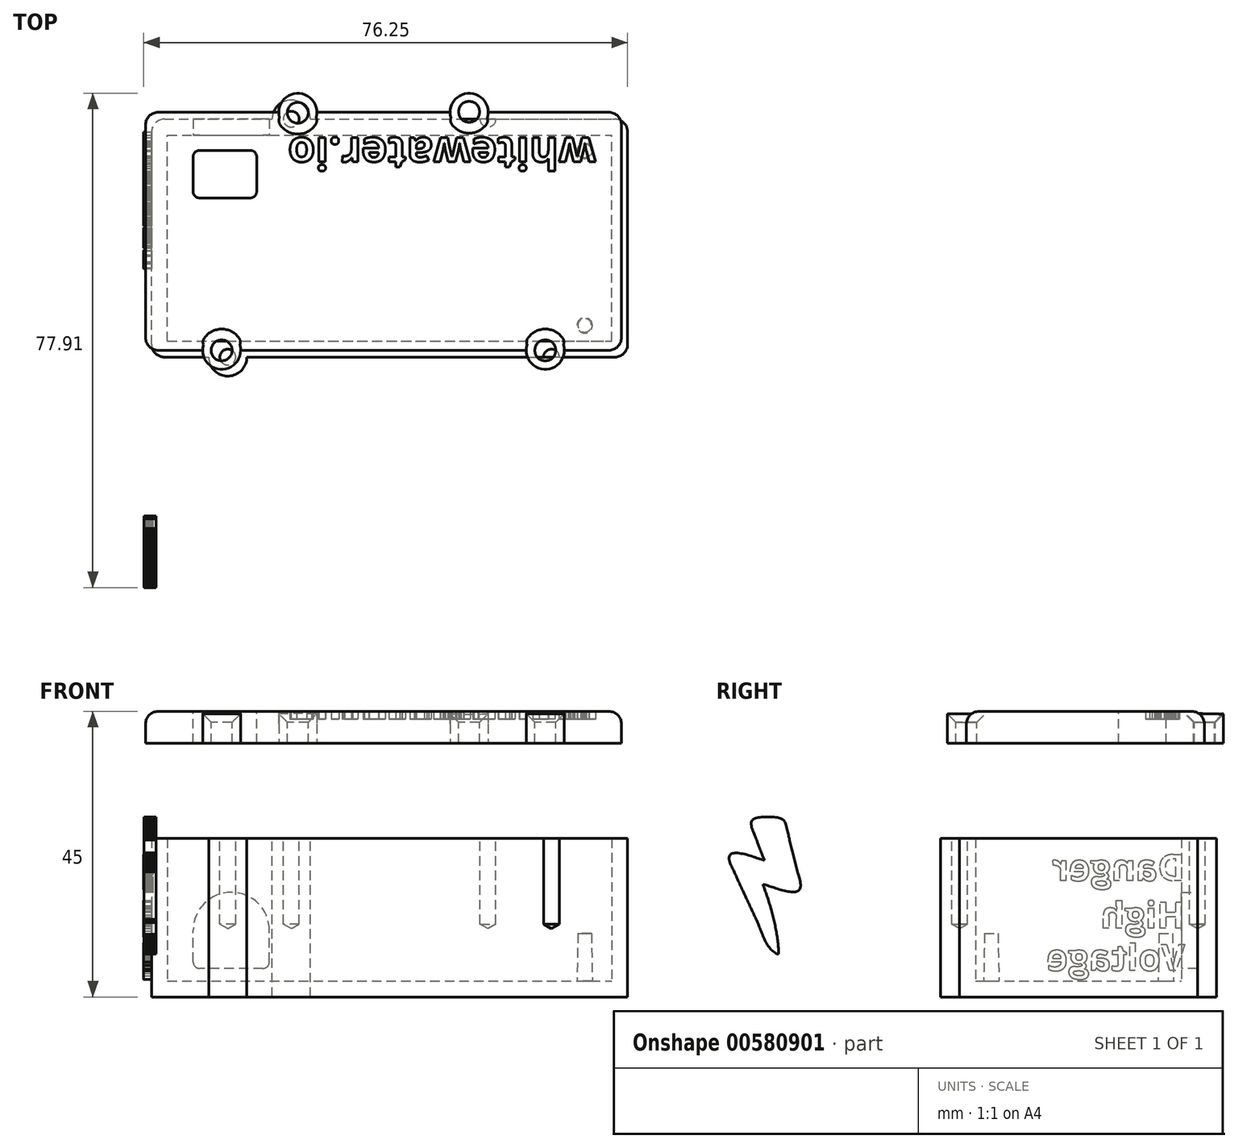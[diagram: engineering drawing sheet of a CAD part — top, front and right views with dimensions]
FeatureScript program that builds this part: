
annotation { "Feature Type Name" : "Feature", "Feature Type Description" : "" }
export const myFeature = defineFeature(function(context is Context, id is Id, definition is map)
    precondition{}
    {
        {
            var Q0;
            Q0=qCreatedBy(makeId("Front.planeOp"),FACE);
            var sketch = newSketch(context, id + "F0", { "sketchPlane" : qUnion([Q0])});
            skLineSegment(sketch, "E0.bottom", {"start": v(-37.5, -18.75) * mm, "end": v(37.5, -18.75) * mm});
            skLineSegment(sketch, "E0.top", {"start": v(-37.5, 18.75) * mm, "end": v(37.5, 18.75) * mm});
            skLineSegment(sketch, "E0.left", {"start": v(-37.5, -18.75) * mm, "end": v(-37.5, 18.75) * mm});
            skLineSegment(sketch, "E0.right", {"start": v(37.5, -18.75) * mm, "end": v(37.5, 18.75) * mm});
            skSolve(sketch);
        }
        {
            var Q0;
            Q0 = qSketchRegion(id + "F0", true);
            extrude(context, id + "F1", {"entities" : qUnion([Q0]), "depth" : 25 * mm, "offsetDistance" : 25 * mm});
        }
        {
            var Q0;
            Q0=makeQuery(id+"F1.opExtrude","CAP_FACE",FACE,{"disambiguationData":[OSD([sQuery(id+"F0.wireOp",EDGE,"E0.bottom"),sQuery(id+"F0.wireOp",EDGE,"E0.top"),sQuery(id+"F0.wireOp",EDGE,"E0.left"),sQuery(id+"F0.wireOp",EDGE,"E0.right")])],"isStart":false});
            shell(context, id + "F2", {"entities" : qUnion([Q0]), "thickness" : 2.5 * mm});
        }
        {
            var Q0;
            Q0=makeQuery(id+"F1.opExtrude","SWEPT_EDGE",EDGE,{"disambiguationData":[OSD([sQuery(id+"F0.wireOp",EDGE,"E0.bottom"),sQuery(id+"F0.wireOp",EDGE,"E0.left")])]});
            var Q1;
            Q1=makeQuery(id+"F1.opExtrude","SWEPT_EDGE",EDGE,{"disambiguationData":[OSD([sQuery(id+"F0.wireOp",EDGE,"E0.top"),sQuery(id+"F0.wireOp",EDGE,"E0.right")])]});
            var Q2;
            Q2=makeQuery(id+"F1.opExtrude","SWEPT_EDGE",EDGE,{"disambiguationData":[OSD([sQuery(id+"F0.wireOp",EDGE,"E0.bottom"),sQuery(id+"F0.wireOp",EDGE,"E0.right")])]});
            var Q3;
            Q3=makeQuery(id+"F1.opExtrude","SWEPT_EDGE",EDGE,{"disambiguationData":[OSD([sQuery(id+"F0.wireOp",EDGE,"E0.top"),sQuery(id+"F0.wireOp",EDGE,"E0.left")])]});
            fillet(context, id + "F3", {"entities" : qUnion([Q0, Q1, Q2, Q3]), "radius" : 2 * mm, "tangentPropagation" : true, "allowEdgeOverflow" : false});
        }
        {
            var Q0;
            Q0=makeQuery(id+"F2.opShell","OFFSET_FACE",FACE,{"disambiguationData":[OSD([sQuery(id+"F0.wireOp",EDGE,"E0.bottom"),sQuery(id+"F0.wireOp",EDGE,"E0.top"),sQuery(id+"F0.wireOp",EDGE,"E0.left"),sQuery(id+"F0.wireOp",EDGE,"E0.right")])]});
            var sketch = newSketch(context, id + "F4", { "sketchPlane" : qUnion([Q0])});
            skLineSegment(sketch, "E1.bottom", {"start": v(-32, 15.5) * mm, "end": v(32, 15.5) * mm, "construction": true});
            skLineSegment(sketch, "E1.top", {"start": v(-32, -15.5) * mm, "end": v(32, -15.5) * mm, "construction": true});
            skLineSegment(sketch, "E1.left", {"start": v(-32, 15.5) * mm, "end": v(-32, -15.5) * mm, "construction": true});
            skLineSegment(sketch, "E1.right", {"start": v(32, 15.5) * mm, "end": v(32, -15.5) * mm, "construction": true});
            skPoint(sketch, "E2", {"position": v(30.75, 13.75) * mm});
            skPoint(sketch, "E3.MirrorP", {"position": v(30.75, -13.75) * mm});
            skCircle(sketch, "E4", {"center": v(30.75, 13.75) * mm, "radius": 1.2 * mm});
            skCircle(sketch, "E5", {"center": v(30.75, -13.75) * mm, "radius": 1.2 * mm});
            skSolve(sketch);
        }
        {
            var Q0;
            Q0=makeQuery(id+"F4.imprint","IMPRINT",FACE,{"disambiguationData":[TD([[makeQuery(id+"F4.imprint","IMPRINT",EDGE,{"derivedFrom":sQuery(id+"F4.wireOp",EDGE,"E5")}),1.0]])]});
            var Q1;
            Q1=makeQuery(id+"F4.imprint","IMPRINT",FACE,{"disambiguationData":[TD([[makeQuery(id+"F4.imprint","IMPRINT",EDGE,{"derivedFrom":sQuery(id+"F4.wireOp",EDGE,"E4")}),1.0]])]});
            extrude(context, id + "F5", {"entities" : qUnion([Q0, Q1]), "operationType" : NewBodyOperationType.ADD, "depth" : 7.5 * mm, "offsetDistance" : 25 * mm, "hasDraft" : true, "draftAngle" : 1 * degree, "draftPullDirection" : true});
        }
        {
            var Q0;
            Q0=makeQuery(id+"F1.opExtrude","SWEPT_FACE",FACE,{"disambiguationData":[OSD([sQuery(id+"F0.wireOp",EDGE,"E0.left")])]});
            var sketch = newSketch(context, id + "F6", { "sketchPlane" : qUnion([Q0])});
            skLineSegment(sketch, "E6", {"start": v(1, 1) * mm, "end": v(0.67, 0.13) * mm});
            skLineSegment(sketch, "E7", {"start": v(0.67, 0.13) * mm, "end": v(0.35, -0.76) * mm});
            skLineSegment(sketch, "E8", {"start": v(0.35, -0.76) * mm, "end": v(0.02, -1.66) * mm});
            skLineSegment(sketch, "E9", {"start": v(0.02, -1.66) * mm, "end": v(-0.3, -2.56) * mm});
            skLineSegment(sketch, "E10", {"start": v(-0.3, -2.56) * mm, "end": v(-0.63, -3.48) * mm});
            skLineSegment(sketch, "E11", {"start": v(-0.63, -3.48) * mm, "end": v(-0.95, -4.4) * mm});
            skLineSegment(sketch, "E12", {"start": v(-0.95, -4.4) * mm, "end": v(-1.27, -5.34) * mm});
            skLineSegment(sketch, "E13", {"start": v(-1.27, -5.34) * mm, "end": v(-1.59, -6.29) * mm});
            skLineSegment(sketch, "E14", {"start": v(-1.59, -6.29) * mm, "end": v(-1.9, -7.24) * mm});
            skLineSegment(sketch, "E15", {"start": v(-1.9, -7.24) * mm, "end": v(-2.21, -8.2) * mm});
            skLineSegment(sketch, "E16", {"start": v(-2.21, -8.2) * mm, "end": v(-2.52, -9.17) * mm});
            skLineSegment(sketch, "E17", {"start": v(-2.52, -9.17) * mm, "end": v(-2.82, -10.14) * mm});
            skLineSegment(sketch, "E18", {"start": v(-2.82, -10.14) * mm, "end": v(-3.12, -11.12) * mm});
            skLineSegment(sketch, "E19", {"start": v(-3.12, -11.12) * mm, "end": v(-3.42, -12.1) * mm});
            skLineSegment(sketch, "E20", {"start": v(-3.42, -12.1) * mm, "end": v(-3.71, -13.1) * mm});
            skLineSegment(sketch, "E21", {"start": v(-3.71, -13.1) * mm, "end": v(-4, -14.1) * mm});
            skLineSegment(sketch, "E22", {"start": v(-4, -14.1) * mm, "end": v(-4.28, -15.1) * mm});
            skLineSegment(sketch, "E23", {"start": v(-4.28, -15.1) * mm, "end": v(-4.56, -16.1) * mm});
            skLineSegment(sketch, "E24", {"start": v(-4.56, -16.1) * mm, "end": v(-4.83, -17.1) * mm});
            skLineSegment(sketch, "E25", {"start": v(-4.83, -17.1) * mm, "end": v(-5.1, -18.12) * mm});
            skLineSegment(sketch, "E26", {"start": v(-5.1, -18.12) * mm, "end": v(-5.36, -19.13) * mm});
            skLineSegment(sketch, "E27", {"start": v(-5.36, -19.13) * mm, "end": v(-5.61, -20.15) * mm});
            skLineSegment(sketch, "E28", {"start": v(-5.61, -20.15) * mm, "end": v(-5.86, -21.16) * mm});
            skLineSegment(sketch, "E29", {"start": v(-5.86, -21.16) * mm, "end": v(-6.1, -22.18) * mm});
            skLineSegment(sketch, "E30", {"start": v(-6.1, -22.18) * mm, "end": v(-6.33, -23.2) * mm});
            skLineSegment(sketch, "E31", {"start": v(-6.33, -23.2) * mm, "end": v(-6.55, -24.22) * mm});
            skLineSegment(sketch, "E32", {"start": v(-6.55, -24.22) * mm, "end": v(-6.77, -25.24) * mm});
            skLineSegment(sketch, "E33", {"start": v(-6.77, -25.24) * mm, "end": v(-6.98, -26.26) * mm});
            skLineSegment(sketch, "E34", {"start": v(-6.98, -26.26) * mm, "end": v(-7.18, -27.27) * mm});
            skLineSegment(sketch, "E35", {"start": v(-7.18, -27.27) * mm, "end": v(-7.37, -28.29) * mm});
            skLineSegment(sketch, "E36", {"start": v(-7.37, -28.29) * mm, "end": v(-7.55, -29.3) * mm});
            skLineSegment(sketch, "E37", {"start": v(-7.55, -29.3) * mm, "end": v(-7.73, -30.31) * mm});
            skLineSegment(sketch, "E38", {"start": v(-7.73, -30.31) * mm, "end": v(-7.9, -31.32) * mm});
            skLineSegment(sketch, "E39", {"start": v(-7.9, -31.32) * mm, "end": v(-8.04, -32.32) * mm});
            skLineSegment(sketch, "E40", {"start": v(-8.04, -32.32) * mm, "end": v(-8.19, -33.32) * mm});
            skLineSegment(sketch, "E41", {"start": v(-8.19, -33.32) * mm, "end": v(-8.32, -34.32) * mm});
            skLineSegment(sketch, "E42", {"start": v(-8.32, -34.32) * mm, "end": v(-8.44, -35.3) * mm});
            skLineSegment(sketch, "E43", {"start": v(-8.44, -35.3) * mm, "end": v(-8.55, -36.3) * mm});
            skLineSegment(sketch, "E44", {"start": v(-8.55, -36.3) * mm, "end": v(-8.65, -37.27) * mm});
            skLineSegment(sketch, "E45", {"start": v(-8.65, -37.27) * mm, "end": v(-8.74, -38.25) * mm});
            skLineSegment(sketch, "E46", {"start": v(-8.74, -38.25) * mm, "end": v(-8.82, -39.21) * mm});
            skLineSegment(sketch, "E47", {"start": v(-8.82, -39.21) * mm, "end": v(-8.88, -40.17) * mm});
            skLineSegment(sketch, "E48", {"start": v(-8.88, -40.17) * mm, "end": v(-8.94, -41.12) * mm});
            skLineSegment(sketch, "E49", {"start": v(-8.94, -41.12) * mm, "end": v(-8.97, -42.07) * mm});
            skLineSegment(sketch, "E50", {"start": v(-8.97, -42.07) * mm, "end": v(-9, -43) * mm});
            skLineSegment(sketch, "E51", {"start": v(-9, -43) * mm, "end": v(-8.22, -42.82) * mm});
            skLineSegment(sketch, "E52", {"start": v(-8.22, -42.82) * mm, "end": v(-7.46, -42.55) * mm});
            skLineSegment(sketch, "E53", {"start": v(-7.46, -42.55) * mm, "end": v(-6.74, -42.2) * mm});
            skLineSegment(sketch, "E54", {"start": v(-6.74, -42.2) * mm, "end": v(-6.04, -41.77) * mm});
            skLineSegment(sketch, "E55", {"start": v(-6.04, -41.77) * mm, "end": v(-5.37, -41.27) * mm});
            skLineSegment(sketch, "E56", {"start": v(-5.37, -41.27) * mm, "end": v(-4.73, -40.7) * mm});
            skLineSegment(sketch, "E57", {"start": v(-4.73, -40.7) * mm, "end": v(-4.1, -40.07) * mm});
            skLineSegment(sketch, "E58", {"start": v(-4.1, -40.07) * mm, "end": v(-3.5, -39.39) * mm});
            skLineSegment(sketch, "E59", {"start": v(-3.5, -39.39) * mm, "end": v(-2.93, -38.65) * mm});
            skLineSegment(sketch, "E60", {"start": v(-2.93, -38.65) * mm, "end": v(-2.38, -37.87) * mm});
            skLineSegment(sketch, "E61", {"start": v(-2.38, -37.87) * mm, "end": v(-1.85, -37.04) * mm});
            skLineSegment(sketch, "E62", {"start": v(-1.85, -37.04) * mm, "end": v(-1.34, -36.18) * mm});
            skLineSegment(sketch, "E63", {"start": v(-1.34, -36.18) * mm, "end": v(-0.84, -35.29) * mm});
            skLineSegment(sketch, "E64", {"start": v(-0.84, -35.29) * mm, "end": v(-0.37, -34.37) * mm});
            skLineSegment(sketch, "E65", {"start": v(-0.37, -34.37) * mm, "end": v(0.1, -33.43) * mm});
            skLineSegment(sketch, "E66", {"start": v(0.1, -33.43) * mm, "end": v(0.53, -32.48) * mm});
            skLineSegment(sketch, "E67", {"start": v(0.53, -32.48) * mm, "end": v(0.96, -31.52) * mm});
            skLineSegment(sketch, "E68", {"start": v(0.96, -31.52) * mm, "end": v(1.37, -30.55) * mm});
            skLineSegment(sketch, "E69", {"start": v(1.37, -30.55) * mm, "end": v(1.77, -29.58) * mm});
            skLineSegment(sketch, "E70", {"start": v(1.77, -29.58) * mm, "end": v(2.16, -28.61) * mm});
            skLineSegment(sketch, "E71", {"start": v(2.16, -28.61) * mm, "end": v(2.53, -27.66) * mm});
            skLineSegment(sketch, "E72", {"start": v(2.53, -27.66) * mm, "end": v(2.9, -26.72) * mm});
            skLineSegment(sketch, "E73", {"start": v(2.9, -26.72) * mm, "end": v(3.25, -25.8) * mm});
            skLineSegment(sketch, "E74", {"start": v(3.25, -25.8) * mm, "end": v(3.6, -24.9) * mm});
            skLineSegment(sketch, "E75", {"start": v(3.6, -24.9) * mm, "end": v(3.93, -24.05) * mm});
            skLineSegment(sketch, "E76", {"start": v(3.93, -24.05) * mm, "end": v(4.26, -23.22) * mm});
            skLineSegment(sketch, "E77", {"start": v(4.26, -23.22) * mm, "end": v(4.59, -22.43) * mm});
            skLineSegment(sketch, "E78", {"start": v(4.59, -22.43) * mm, "end": v(4.9, -21.69) * mm});
            skLineSegment(sketch, "E79", {"start": v(4.9, -21.69) * mm, "end": v(5.22, -21) * mm});
            skLineSegment(sketch, "E80", {"start": v(5.22, -21) * mm, "end": v(5.65, -20.1) * mm});
            skLineSegment(sketch, "E81", {"start": v(5.65, -20.1) * mm, "end": v(6.07, -19.2) * mm});
            skLineSegment(sketch, "E82", {"start": v(6.07, -19.2) * mm, "end": v(6.5, -18.29) * mm});
            skLineSegment(sketch, "E83", {"start": v(6.5, -18.29) * mm, "end": v(6.93, -17.38) * mm});
            skLineSegment(sketch, "E84", {"start": v(6.93, -17.38) * mm, "end": v(7.36, -16.47) * mm});
            skLineSegment(sketch, "E85", {"start": v(7.36, -16.47) * mm, "end": v(7.79, -15.57) * mm});
            skLineSegment(sketch, "E86", {"start": v(7.79, -15.57) * mm, "end": v(8.21, -14.66) * mm});
            skLineSegment(sketch, "E87", {"start": v(8.21, -14.66) * mm, "end": v(8.64, -13.76) * mm});
            skLineSegment(sketch, "E88", {"start": v(8.64, -13.76) * mm, "end": v(9.07, -12.85) * mm});
            skLineSegment(sketch, "E89", {"start": v(9.07, -12.85) * mm, "end": v(9.5, -11.94) * mm});
            skLineSegment(sketch, "E90", {"start": v(9.5, -11.94) * mm, "end": v(9.92, -11.03) * mm});
            skLineSegment(sketch, "E91", {"start": v(9.92, -11.03) * mm, "end": v(10.35, -10.13) * mm});
            skLineSegment(sketch, "E92", {"start": v(10.35, -10.13) * mm, "end": v(10.77, -9.22) * mm});
            skLineSegment(sketch, "E93", {"start": v(10.77, -9.22) * mm, "end": v(11.2, -8.3) * mm});
            skLineSegment(sketch, "E94", {"start": v(11.2, -8.3) * mm, "end": v(11.63, -7.4) * mm});
            skLineSegment(sketch, "E95", {"start": v(11.63, -7.4) * mm, "end": v(12.05, -6.5) * mm});
            skLineSegment(sketch, "E96", {"start": v(12.05, -6.5) * mm, "end": v(12.48, -5.58) * mm});
            skLineSegment(sketch, "E97", {"start": v(12.48, -5.58) * mm, "end": v(12.9, -4.67) * mm});
            skLineSegment(sketch, "E98", {"start": v(12.9, -4.67) * mm, "end": v(13.32, -3.76) * mm});
            skLineSegment(sketch, "E99", {"start": v(13.32, -3.76) * mm, "end": v(13.74, -2.85) * mm});
            skLineSegment(sketch, "E100", {"start": v(13.74, -2.85) * mm, "end": v(14.16, -1.94) * mm});
            skLineSegment(sketch, "E101", {"start": v(14.16, -1.94) * mm, "end": v(14.59, -1.03) * mm});
            skLineSegment(sketch, "E102", {"start": v(14.59, -1.03) * mm, "end": v(15, -0.12) * mm});
            skLineSegment(sketch, "E103", {"start": v(15, -0.12) * mm, "end": v(15.42, 0.79) * mm});
            skLineSegment(sketch, "E104", {"start": v(15.42, 0.79) * mm, "end": v(15.84, 1.7) * mm});
            skLineSegment(sketch, "E105", {"start": v(15.84, 1.7) * mm, "end": v(16.26, 2.61) * mm});
            skLineSegment(sketch, "E106", {"start": v(16.26, 2.61) * mm, "end": v(16.67, 3.52) * mm});
            skLineSegment(sketch, "E107", {"start": v(16.67, 3.52) * mm, "end": v(17.09, 4.43) * mm});
            skLineSegment(sketch, "E108", {"start": v(17.09, 4.43) * mm, "end": v(17.5, 5.35) * mm});
            skLineSegment(sketch, "E109", {"start": v(17.5, 5.35) * mm, "end": v(17.91, 6.26) * mm});
            skLineSegment(sketch, "E110", {"start": v(17.91, 6.26) * mm, "end": v(18.32, 7.17) * mm});
            skLineSegment(sketch, "E111", {"start": v(18.32, 7.17) * mm, "end": v(18.73, 8.09) * mm});
            skLineSegment(sketch, "E112", {"start": v(18.73, 8.09) * mm, "end": v(19.14, 9) * mm});
            skLineSegment(sketch, "E113", {"start": v(19.14, 9) * mm, "end": v(19.43, 9.61) * mm});
            skLineSegment(sketch, "E114", {"start": v(19.43, 9.61) * mm, "end": v(19.8, 10.34) * mm});
            skLineSegment(sketch, "E115", {"start": v(19.8, 10.34) * mm, "end": v(20.21, 11.17) * mm});
            skLineSegment(sketch, "E116", {"start": v(20.21, 11.17) * mm, "end": v(20.66, 12.08) * mm});
            skLineSegment(sketch, "E117", {"start": v(20.66, 12.08) * mm, "end": v(21.1, 13.03) * mm});
            skLineSegment(sketch, "E118", {"start": v(21.1, 13.03) * mm, "end": v(21.5, 14.02) * mm});
            skLineSegment(sketch, "E119", {"start": v(21.5, 14.02) * mm, "end": v(21.86, 15.02) * mm});
            skLineSegment(sketch, "E120", {"start": v(21.86, 15.02) * mm, "end": v(22.14, 16) * mm});
            skLineSegment(sketch, "E121", {"start": v(22.14, 16) * mm, "end": v(22.3, 16.95) * mm});
            skLineSegment(sketch, "E122", {"start": v(22.3, 16.95) * mm, "end": v(22.33, 17.84) * mm});
            skLineSegment(sketch, "E123", {"start": v(22.33, 17.84) * mm, "end": v(22.2, 18.64) * mm});
            skLineSegment(sketch, "E124", {"start": v(22.2, 18.64) * mm, "end": v(21.88, 19.35) * mm});
            skLineSegment(sketch, "E125", {"start": v(21.88, 19.35) * mm, "end": v(21.35, 19.93) * mm});
            skLineSegment(sketch, "E126", {"start": v(21.35, 19.93) * mm, "end": v(20.8, 20.27) * mm});
            skLineSegment(sketch, "E127", {"start": v(20.8, 20.27) * mm, "end": v(20.16, 20.52) * mm});
            skLineSegment(sketch, "E128", {"start": v(20.16, 20.52) * mm, "end": v(19.43, 20.69) * mm});
            skLineSegment(sketch, "E129", {"start": v(19.43, 20.69) * mm, "end": v(18.62, 20.77) * mm});
            skLineSegment(sketch, "E130", {"start": v(18.62, 20.77) * mm, "end": v(17.73, 20.78) * mm});
            skLineSegment(sketch, "E131", {"start": v(17.73, 20.78) * mm, "end": v(16.78, 20.73) * mm});
            skLineSegment(sketch, "E132", {"start": v(16.78, 20.73) * mm, "end": v(15.78, 20.61) * mm});
            skLineSegment(sketch, "E133", {"start": v(15.78, 20.61) * mm, "end": v(14.74, 20.45) * mm});
            skLineSegment(sketch, "E134", {"start": v(14.74, 20.45) * mm, "end": v(13.65, 20.23) * mm});
            skLineSegment(sketch, "E135", {"start": v(13.65, 20.23) * mm, "end": v(12.55, 19.98) * mm});
            skLineSegment(sketch, "E136", {"start": v(12.55, 19.98) * mm, "end": v(11.43, 19.7) * mm});
            skLineSegment(sketch, "E137", {"start": v(11.43, 19.7) * mm, "end": v(10.3, 19.38) * mm});
            skLineSegment(sketch, "E138", {"start": v(10.3, 19.38) * mm, "end": v(9.17, 19.04) * mm});
            skLineSegment(sketch, "E139", {"start": v(9.17, 19.04) * mm, "end": v(8.05, 18.7) * mm});
            skLineSegment(sketch, "E140", {"start": v(8.05, 18.7) * mm, "end": v(6.95, 18.34) * mm});
            skLineSegment(sketch, "E141", {"start": v(6.95, 18.34) * mm, "end": v(5.88, 17.98) * mm});
            skLineSegment(sketch, "E142", {"start": v(5.88, 17.98) * mm, "end": v(4.85, 17.63) * mm});
            skLineSegment(sketch, "E143", {"start": v(4.85, 17.63) * mm, "end": v(3.87, 17.29) * mm});
            skLineSegment(sketch, "E144", {"start": v(3.87, 17.29) * mm, "end": v(2.95, 16.97) * mm});
            skLineSegment(sketch, "E145", {"start": v(2.95, 16.97) * mm, "end": v(2.09, 16.67) * mm});
            skLineSegment(sketch, "E146", {"start": v(2.09, 16.67) * mm, "end": v(1.3, 16.4) * mm});
            skLineSegment(sketch, "E147", {"start": v(1.3, 16.4) * mm, "end": v(0.6, 16.18) * mm});
            skLineSegment(sketch, "E148", {"start": v(0.6, 16.18) * mm, "end": v(0, 16) * mm});
            skLineSegment(sketch, "E149", {"start": v(0, 16) * mm, "end": v(0.39, 17) * mm});
            skLineSegment(sketch, "E150", {"start": v(0.39, 17) * mm, "end": v(0.77, 18) * mm});
            skLineSegment(sketch, "E151", {"start": v(0.77, 18) * mm, "end": v(1.16, 19) * mm});
            skLineSegment(sketch, "E152", {"start": v(1.16, 19) * mm, "end": v(1.54, 20) * mm});
            skLineSegment(sketch, "E153", {"start": v(1.54, 20) * mm, "end": v(1.93, 21) * mm});
            skLineSegment(sketch, "E154", {"start": v(1.93, 21) * mm, "end": v(2.31, 21.99) * mm});
            skLineSegment(sketch, "E155", {"start": v(2.31, 21.99) * mm, "end": v(2.7, 22.99) * mm});
            skLineSegment(sketch, "E156", {"start": v(2.7, 22.99) * mm, "end": v(3.07, 23.99) * mm});
            skLineSegment(sketch, "E157", {"start": v(3.07, 23.99) * mm, "end": v(3.45, 24.99) * mm});
            skLineSegment(sketch, "E158", {"start": v(3.45, 24.99) * mm, "end": v(3.83, 26) * mm});
            skLineSegment(sketch, "E159", {"start": v(3.83, 26) * mm, "end": v(4.2, 27) * mm});
            skLineSegment(sketch, "E160", {"start": v(4.2, 27) * mm, "end": v(4.58, 28) * mm});
            skLineSegment(sketch, "E161", {"start": v(4.58, 28) * mm, "end": v(4.95, 29) * mm});
            skLineSegment(sketch, "E162", {"start": v(4.95, 29) * mm, "end": v(5.26, 29.8) * mm});
            skLineSegment(sketch, "E163", {"start": v(5.26, 29.8) * mm, "end": v(5.63, 30.68) * mm});
            skLineSegment(sketch, "E164", {"start": v(5.63, 30.68) * mm, "end": v(6.05, 31.63) * mm});
            skLineSegment(sketch, "E165", {"start": v(6.05, 31.63) * mm, "end": v(6.49, 32.64) * mm});
            skLineSegment(sketch, "E166", {"start": v(6.49, 32.64) * mm, "end": v(6.92, 33.7) * mm});
            skLineSegment(sketch, "E167", {"start": v(6.92, 33.7) * mm, "end": v(7.34, 34.76) * mm});
            skLineSegment(sketch, "E168", {"start": v(7.34, 34.76) * mm, "end": v(7.7, 35.83) * mm});
            skLineSegment(sketch, "E169", {"start": v(7.7, 35.83) * mm, "end": v(8.02, 36.9) * mm});
            skLineSegment(sketch, "E170", {"start": v(8.02, 36.9) * mm, "end": v(8.24, 37.93) * mm});
            skLineSegment(sketch, "E171", {"start": v(8.24, 37.93) * mm, "end": v(8.36, 38.91) * mm});
            skLineSegment(sketch, "E172", {"start": v(8.36, 38.91) * mm, "end": v(8.35, 39.84) * mm});
            skLineSegment(sketch, "E173", {"start": v(8.35, 39.84) * mm, "end": v(8.19, 40.68) * mm});
            skLineSegment(sketch, "E174", {"start": v(8.19, 40.68) * mm, "end": v(7.95, 41.17) * mm});
            skLineSegment(sketch, "E175", {"start": v(7.95, 41.17) * mm, "end": v(7.57, 41.6) * mm});
            skLineSegment(sketch, "E176", {"start": v(7.57, 41.6) * mm, "end": v(7.05, 41.99) * mm});
            skLineSegment(sketch, "E177", {"start": v(7.05, 41.99) * mm, "end": v(6.4, 42.33) * mm});
            skLineSegment(sketch, "E178", {"start": v(6.4, 42.33) * mm, "end": v(5.65, 42.62) * mm});
            skLineSegment(sketch, "E179", {"start": v(5.65, 42.62) * mm, "end": v(4.8, 42.87) * mm});
            skLineSegment(sketch, "E180", {"start": v(4.8, 42.87) * mm, "end": v(3.86, 43.08) * mm});
            skLineSegment(sketch, "E181", {"start": v(3.86, 43.08) * mm, "end": v(2.85, 43.25) * mm});
            skLineSegment(sketch, "E182", {"start": v(2.85, 43.25) * mm, "end": v(1.78, 43.38) * mm});
            skLineSegment(sketch, "E183", {"start": v(1.78, 43.38) * mm, "end": v(0.68, 43.48) * mm});
            skLineSegment(sketch, "E184", {"start": v(0.68, 43.48) * mm, "end": v(-0.46, 43.53) * mm});
            skLineSegment(sketch, "E185", {"start": v(-0.46, 43.53) * mm, "end": v(-1.6, 43.56) * mm});
            skLineSegment(sketch, "E186", {"start": v(-1.6, 43.56) * mm, "end": v(-2.76, 43.55) * mm});
            skLineSegment(sketch, "E187", {"start": v(-2.76, 43.55) * mm, "end": v(-3.9, 43.5) * mm});
            skLineSegment(sketch, "E188", {"start": v(-3.9, 43.5) * mm, "end": v(-5.02, 43.44) * mm});
            skLineSegment(sketch, "E189", {"start": v(-5.02, 43.44) * mm, "end": v(-6.1, 43.34) * mm});
            skLineSegment(sketch, "E190", {"start": v(-6.1, 43.34) * mm, "end": v(-7.13, 43.21) * mm});
            skLineSegment(sketch, "E191", {"start": v(-7.13, 43.21) * mm, "end": v(-8.09, 43.06) * mm});
            skLineSegment(sketch, "E192", {"start": v(-8.09, 43.06) * mm, "end": v(-8.97, 42.88) * mm});
            skLineSegment(sketch, "E193", {"start": v(-8.97, 42.88) * mm, "end": v(-9.76, 42.69) * mm});
            skLineSegment(sketch, "E194", {"start": v(-9.76, 42.69) * mm, "end": v(-10.44, 42.47) * mm});
            skLineSegment(sketch, "E195", {"start": v(-10.44, 42.47) * mm, "end": v(-11, 42.23) * mm});
            skLineSegment(sketch, "E196", {"start": v(-11, 42.23) * mm, "end": v(-11.44, 41.97) * mm});
            skLineSegment(sketch, "E197", {"start": v(-11.44, 41.97) * mm, "end": v(-12.1, 41.36) * mm});
            skLineSegment(sketch, "E198", {"start": v(-12.1, 41.36) * mm, "end": v(-12.66, 40.6) * mm});
            skLineSegment(sketch, "E199", {"start": v(-12.66, 40.6) * mm, "end": v(-13.12, 39.75) * mm});
            skLineSegment(sketch, "E200", {"start": v(-13.12, 39.75) * mm, "end": v(-13.5, 38.82) * mm});
            skLineSegment(sketch, "E201", {"start": v(-13.5, 38.82) * mm, "end": v(-13.81, 37.83) * mm});
            skLineSegment(sketch, "E202", {"start": v(-13.81, 37.83) * mm, "end": v(-14.07, 36.81) * mm});
            skLineSegment(sketch, "E203", {"start": v(-14.07, 36.81) * mm, "end": v(-14.3, 35.8) * mm});
            skLineSegment(sketch, "E204", {"start": v(-14.3, 35.8) * mm, "end": v(-14.49, 34.8) * mm});
            skLineSegment(sketch, "E205", {"start": v(-14.49, 34.8) * mm, "end": v(-14.68, 33.86) * mm});
            skLineSegment(sketch, "E206", {"start": v(-14.68, 33.86) * mm, "end": v(-14.87, 33) * mm});
            skLineSegment(sketch, "E207", {"start": v(-14.87, 33) * mm, "end": v(-15.12, 32) * mm});
            skLineSegment(sketch, "E208", {"start": v(-15.12, 32) * mm, "end": v(-15.37, 31) * mm});
            skLineSegment(sketch, "E209", {"start": v(-15.37, 31) * mm, "end": v(-15.61, 30) * mm});
            skLineSegment(sketch, "E210", {"start": v(-15.61, 30) * mm, "end": v(-15.85, 29) * mm});
            skLineSegment(sketch, "E211", {"start": v(-15.85, 29) * mm, "end": v(-16.1, 28) * mm});
            skLineSegment(sketch, "E212", {"start": v(-16.1, 28) * mm, "end": v(-16.33, 27) * mm});
            skLineSegment(sketch, "E213", {"start": v(-16.33, 27) * mm, "end": v(-16.57, 26) * mm});
            skLineSegment(sketch, "E214", {"start": v(-16.57, 26) * mm, "end": v(-16.8, 25) * mm});
            skLineSegment(sketch, "E215", {"start": v(-16.8, 25) * mm, "end": v(-17.05, 24) * mm});
            skLineSegment(sketch, "E216", {"start": v(-17.05, 24) * mm, "end": v(-17.28, 22.99) * mm});
            skLineSegment(sketch, "E217", {"start": v(-17.28, 22.99) * mm, "end": v(-17.52, 21.99) * mm});
            skLineSegment(sketch, "E218", {"start": v(-17.52, 21.99) * mm, "end": v(-17.76, 20.98) * mm});
            skLineSegment(sketch, "E219", {"start": v(-17.76, 20.98) * mm, "end": v(-18, 19.98) * mm});
            skLineSegment(sketch, "E220", {"start": v(-18, 19.98) * mm, "end": v(-18.24, 18.98) * mm});
            skLineSegment(sketch, "E221", {"start": v(-18.24, 18.98) * mm, "end": v(-18.48, 17.98) * mm});
            skLineSegment(sketch, "E222", {"start": v(-18.48, 17.98) * mm, "end": v(-18.72, 16.97) * mm});
            skLineSegment(sketch, "E223", {"start": v(-18.72, 16.97) * mm, "end": v(-18.96, 15.97) * mm});
            skLineSegment(sketch, "E224", {"start": v(-18.96, 15.97) * mm, "end": v(-19.2, 14.97) * mm});
            skLineSegment(sketch, "E225", {"start": v(-19.2, 14.97) * mm, "end": v(-19.46, 13.97) * mm});
            skLineSegment(sketch, "E226", {"start": v(-19.46, 13.97) * mm, "end": v(-19.7, 12.98) * mm});
            skLineSegment(sketch, "E227", {"start": v(-19.7, 12.98) * mm, "end": v(-19.96, 11.98) * mm});
            skLineSegment(sketch, "E228", {"start": v(-19.96, 11.98) * mm, "end": v(-20.22, 10.98) * mm});
            skLineSegment(sketch, "E229", {"start": v(-20.22, 10.98) * mm, "end": v(-20.48, 9.99) * mm});
            skLineSegment(sketch, "E230", {"start": v(-20.48, 9.99) * mm, "end": v(-20.74, 9) * mm});
            skLineSegment(sketch, "E231", {"start": v(-20.74, 9) * mm, "end": v(-21.01, 8) * mm});
            skLineSegment(sketch, "E232", {"start": v(-21.01, 8) * mm, "end": v(-21.21, 7.31) * mm});
            skLineSegment(sketch, "E233", {"start": v(-21.21, 7.31) * mm, "end": v(-21.46, 6.53) * mm});
            skLineSegment(sketch, "E234", {"start": v(-21.46, 6.53) * mm, "end": v(-21.74, 5.67) * mm});
            skLineSegment(sketch, "E235", {"start": v(-21.74, 5.67) * mm, "end": v(-22.02, 4.75) * mm});
            skLineSegment(sketch, "E236", {"start": v(-22.02, 4.75) * mm, "end": v(-22.28, 3.8) * mm});
            skLineSegment(sketch, "E237", {"start": v(-22.28, 3.8) * mm, "end": v(-22.51, 2.82) * mm});
            skLineSegment(sketch, "E238", {"start": v(-22.51, 2.82) * mm, "end": v(-22.69, 1.84) * mm});
            skLineSegment(sketch, "E239", {"start": v(-22.69, 1.84) * mm, "end": v(-22.78, 0.89) * mm});
            skLineSegment(sketch, "E240", {"start": v(-22.78, 0.89) * mm, "end": v(-22.78, -0.03) * mm});
            skLineSegment(sketch, "E241", {"start": v(-22.78, -0.03) * mm, "end": v(-22.66, -0.9) * mm});
            skLineSegment(sketch, "E242", {"start": v(-22.66, -0.9) * mm, "end": v(-22.4, -1.67) * mm});
            skLineSegment(sketch, "E243", {"start": v(-22.4, -1.67) * mm, "end": v(-21.99, -2.36) * mm});
            skLineSegment(sketch, "E244", {"start": v(-21.99, -2.36) * mm, "end": v(-21.4, -2.93) * mm});
            skLineSegment(sketch, "E245", {"start": v(-21.4, -2.93) * mm, "end": v(-20.83, -3.27) * mm});
            skLineSegment(sketch, "E246", {"start": v(-20.83, -3.27) * mm, "end": v(-20.17, -3.52) * mm});
            skLineSegment(sketch, "E247", {"start": v(-20.17, -3.52) * mm, "end": v(-19.43, -3.68) * mm});
            skLineSegment(sketch, "E248", {"start": v(-19.43, -3.68) * mm, "end": v(-18.62, -3.77) * mm});
            skLineSegment(sketch, "E249", {"start": v(-18.62, -3.77) * mm, "end": v(-17.74, -3.79) * mm});
            skLineSegment(sketch, "E250", {"start": v(-17.74, -3.79) * mm, "end": v(-16.8, -3.75) * mm});
            skLineSegment(sketch, "E251", {"start": v(-16.8, -3.75) * mm, "end": v(-15.83, -3.64) * mm});
            skLineSegment(sketch, "E252", {"start": v(-15.83, -3.64) * mm, "end": v(-14.8, -3.49) * mm});
            skLineSegment(sketch, "E253", {"start": v(-14.8, -3.49) * mm, "end": v(-13.74, -3.3) * mm});
            skLineSegment(sketch, "E254", {"start": v(-13.74, -3.3) * mm, "end": v(-12.65, -3.05) * mm});
            skLineSegment(sketch, "E255", {"start": v(-12.65, -3.05) * mm, "end": v(-11.54, -2.78) * mm});
            skLineSegment(sketch, "E256", {"start": v(-11.54, -2.78) * mm, "end": v(-10.43, -2.48) * mm});
            skLineSegment(sketch, "E257", {"start": v(-10.43, -2.48) * mm, "end": v(-9.3, -2.16) * mm});
            skLineSegment(sketch, "E258", {"start": v(-9.3, -2.16) * mm, "end": v(-8.19, -1.83) * mm});
            skLineSegment(sketch, "E259", {"start": v(-8.19, -1.83) * mm, "end": v(-7.09, -1.48) * mm});
            skLineSegment(sketch, "E260", {"start": v(-7.09, -1.48) * mm, "end": v(-6, -1.14) * mm});
            skLineSegment(sketch, "E261", {"start": v(-6, -1.14) * mm, "end": v(-4.95, -0.8) * mm});
            skLineSegment(sketch, "E262", {"start": v(-4.95, -0.8) * mm, "end": v(-3.93, -0.46) * mm});
            skLineSegment(sketch, "E263", {"start": v(-3.93, -0.46) * mm, "end": v(-2.95, -0.14) * mm});
            skLineSegment(sketch, "E264", {"start": v(-2.95, -0.14) * mm, "end": v(-2.03, 0.15) * mm});
            skLineSegment(sketch, "E265", {"start": v(-2.03, 0.15) * mm, "end": v(-1.16, 0.42) * mm});
            skLineSegment(sketch, "E266", {"start": v(-1.16, 0.42) * mm, "end": v(-0.36, 0.66) * mm});
            skLineSegment(sketch, "E267", {"start": v(-0.36, 0.66) * mm, "end": v(0.36, 0.85) * mm});
            skLineSegment(sketch, "E268", {"start": v(0.36, 0.85) * mm, "end": v(1, 1) * mm});
            skSolve(sketch);
        }
        {
            var Q0;
            Q0 = qSketchRegion(id + "F6", true);
            var Q1;
            Q1=makeQuery(id+"F6.imprint","IMPRINT",FACE,{"disambiguationData":[TD([[makeQuery(id+"F6.imprint","IMPRINT",EDGE,{"derivedFrom":sQuery(id+"F6.wireOp",EDGE,"E6")}),1.0]])]});
            extrude(context, id + "F7", {"entities" : qUnion([Q0, Q1]), "depth" : 7.5 * mm, "offsetDistance" : 25 * mm});
        }
        {
            var Q0;
            Q0=makeQuery(id+"F7.opExtrude","SWEPT_BODY",BODY,{"disambiguationData":[OSD([sQuery(id+"F6.wireOp",EDGE,"E6"),sQuery(id+"F6.wireOp",EDGE,"E7"),sQuery(id+"F6.wireOp",EDGE,"E8"),sQuery(id+"F6.wireOp",EDGE,"E9"),sQuery(id+"F6.wireOp",EDGE,"E10"),sQuery(id+"F6.wireOp",EDGE,"E11"),sQuery(id+"F6.wireOp",EDGE,"E12"),sQuery(id+"F6.wireOp",EDGE,"E13"),sQuery(id+"F6.wireOp",EDGE,"E14"),sQuery(id+"F6.wireOp",EDGE,"E15"),sQuery(id+"F6.wireOp",EDGE,"E16"),sQuery(id+"F6.wireOp",EDGE,"E17"),sQuery(id+"F6.wireOp",EDGE,"E18"),sQuery(id+"F6.wireOp",EDGE,"E19"),sQuery(id+"F6.wireOp",EDGE,"E20"),sQuery(id+"F6.wireOp",EDGE,"E21"),sQuery(id+"F6.wireOp",EDGE,"E22"),sQuery(id+"F6.wireOp",EDGE,"E23"),sQuery(id+"F6.wireOp",EDGE,"E24"),sQuery(id+"F6.wireOp",EDGE,"E25"),sQuery(id+"F6.wireOp",EDGE,"E26"),sQuery(id+"F6.wireOp",EDGE,"E27"),sQuery(id+"F6.wireOp",EDGE,"E28"),sQuery(id+"F6.wireOp",EDGE,"E29"),sQuery(id+"F6.wireOp",EDGE,"E30"),sQuery(id+"F6.wireOp",EDGE,"E31"),sQuery(id+"F6.wireOp",EDGE,"E32"),sQuery(id+"F6.wireOp",EDGE,"E33"),sQuery(id+"F6.wireOp",EDGE,"E34"),sQuery(id+"F6.wireOp",EDGE,"E35"),sQuery(id+"F6.wireOp",EDGE,"E36"),sQuery(id+"F6.wireOp",EDGE,"E37"),sQuery(id+"F6.wireOp",EDGE,"E38"),sQuery(id+"F6.wireOp",EDGE,"E39"),sQuery(id+"F6.wireOp",EDGE,"E40"),sQuery(id+"F6.wireOp",EDGE,"E41"),sQuery(id+"F6.wireOp",EDGE,"E42"),sQuery(id+"F6.wireOp",EDGE,"E43"),sQuery(id+"F6.wireOp",EDGE,"E44"),sQuery(id+"F6.wireOp",EDGE,"E45"),sQuery(id+"F6.wireOp",EDGE,"E46"),sQuery(id+"F6.wireOp",EDGE,"E47"),sQuery(id+"F6.wireOp",EDGE,"E48"),sQuery(id+"F6.wireOp",EDGE,"E49"),sQuery(id+"F6.wireOp",EDGE,"E50"),sQuery(id+"F6.wireOp",EDGE,"E51"),sQuery(id+"F6.wireOp",EDGE,"E52"),sQuery(id+"F6.wireOp",EDGE,"E53"),sQuery(id+"F6.wireOp",EDGE,"E54"),sQuery(id+"F6.wireOp",EDGE,"E55"),sQuery(id+"F6.wireOp",EDGE,"E56"),sQuery(id+"F6.wireOp",EDGE,"E57"),sQuery(id+"F6.wireOp",EDGE,"E58"),sQuery(id+"F6.wireOp",EDGE,"E59"),sQuery(id+"F6.wireOp",EDGE,"E60"),sQuery(id+"F6.wireOp",EDGE,"E61"),sQuery(id+"F6.wireOp",EDGE,"E62"),sQuery(id+"F6.wireOp",EDGE,"E63"),sQuery(id+"F6.wireOp",EDGE,"E64"),sQuery(id+"F6.wireOp",EDGE,"E65"),sQuery(id+"F6.wireOp",EDGE,"E66"),sQuery(id+"F6.wireOp",EDGE,"E67"),sQuery(id+"F6.wireOp",EDGE,"E68"),sQuery(id+"F6.wireOp",EDGE,"E69"),sQuery(id+"F6.wireOp",EDGE,"E70"),sQuery(id+"F6.wireOp",EDGE,"E71"),sQuery(id+"F6.wireOp",EDGE,"E72"),sQuery(id+"F6.wireOp",EDGE,"E73"),sQuery(id+"F6.wireOp",EDGE,"E74"),sQuery(id+"F6.wireOp",EDGE,"E75"),sQuery(id+"F6.wireOp",EDGE,"E76"),sQuery(id+"F6.wireOp",EDGE,"E77"),sQuery(id+"F6.wireOp",EDGE,"E78"),sQuery(id+"F6.wireOp",EDGE,"E79"),sQuery(id+"F6.wireOp",EDGE,"E80"),sQuery(id+"F6.wireOp",EDGE,"E81"),sQuery(id+"F6.wireOp",EDGE,"E82"),sQuery(id+"F6.wireOp",EDGE,"E83"),sQuery(id+"F6.wireOp",EDGE,"E84"),sQuery(id+"F6.wireOp",EDGE,"E85"),sQuery(id+"F6.wireOp",EDGE,"E86"),sQuery(id+"F6.wireOp",EDGE,"E87"),sQuery(id+"F6.wireOp",EDGE,"E88"),sQuery(id+"F6.wireOp",EDGE,"E89"),sQuery(id+"F6.wireOp",EDGE,"E90"),sQuery(id+"F6.wireOp",EDGE,"E91"),sQuery(id+"F6.wireOp",EDGE,"E92"),sQuery(id+"F6.wireOp",EDGE,"E93"),sQuery(id+"F6.wireOp",EDGE,"E94"),sQuery(id+"F6.wireOp",EDGE,"E95"),sQuery(id+"F6.wireOp",EDGE,"E96"),sQuery(id+"F6.wireOp",EDGE,"E97"),sQuery(id+"F6.wireOp",EDGE,"E98"),sQuery(id+"F6.wireOp",EDGE,"E99"),sQuery(id+"F6.wireOp",EDGE,"E100"),sQuery(id+"F6.wireOp",EDGE,"E101"),sQuery(id+"F6.wireOp",EDGE,"E102"),sQuery(id+"F6.wireOp",EDGE,"E103"),sQuery(id+"F6.wireOp",EDGE,"E104"),sQuery(id+"F6.wireOp",EDGE,"E105"),sQuery(id+"F6.wireOp",EDGE,"E106"),sQuery(id+"F6.wireOp",EDGE,"E107"),sQuery(id+"F6.wireOp",EDGE,"E108"),sQuery(id+"F6.wireOp",EDGE,"E109"),sQuery(id+"F6.wireOp",EDGE,"E110"),sQuery(id+"F6.wireOp",EDGE,"E111"),sQuery(id+"F6.wireOp",EDGE,"E112"),sQuery(id+"F6.wireOp",EDGE,"E113"),sQuery(id+"F6.wireOp",EDGE,"E114"),sQuery(id+"F6.wireOp",EDGE,"E115"),sQuery(id+"F6.wireOp",EDGE,"E116"),sQuery(id+"F6.wireOp",EDGE,"E117"),sQuery(id+"F6.wireOp",EDGE,"E118"),sQuery(id+"F6.wireOp",EDGE,"E119"),sQuery(id+"F6.wireOp",EDGE,"E120"),sQuery(id+"F6.wireOp",EDGE,"E121"),sQuery(id+"F6.wireOp",EDGE,"E122"),sQuery(id+"F6.wireOp",EDGE,"E123"),sQuery(id+"F6.wireOp",EDGE,"E124"),sQuery(id+"F6.wireOp",EDGE,"E125"),sQuery(id+"F6.wireOp",EDGE,"E126"),sQuery(id+"F6.wireOp",EDGE,"E127"),sQuery(id+"F6.wireOp",EDGE,"E128"),sQuery(id+"F6.wireOp",EDGE,"E129"),sQuery(id+"F6.wireOp",EDGE,"E130"),sQuery(id+"F6.wireOp",EDGE,"E131"),sQuery(id+"F6.wireOp",EDGE,"E132"),sQuery(id+"F6.wireOp",EDGE,"E133"),sQuery(id+"F6.wireOp",EDGE,"E134"),sQuery(id+"F6.wireOp",EDGE,"E135"),sQuery(id+"F6.wireOp",EDGE,"E136"),sQuery(id+"F6.wireOp",EDGE,"E137"),sQuery(id+"F6.wireOp",EDGE,"E138"),sQuery(id+"F6.wireOp",EDGE,"E139"),sQuery(id+"F6.wireOp",EDGE,"E140"),sQuery(id+"F6.wireOp",EDGE,"E141"),sQuery(id+"F6.wireOp",EDGE,"E142"),sQuery(id+"F6.wireOp",EDGE,"E143"),sQuery(id+"F6.wireOp",EDGE,"E144"),sQuery(id+"F6.wireOp",EDGE,"E145"),sQuery(id+"F6.wireOp",EDGE,"E146"),sQuery(id+"F6.wireOp",EDGE,"E147"),sQuery(id+"F6.wireOp",EDGE,"E148"),sQuery(id+"F6.wireOp",EDGE,"E149"),sQuery(id+"F6.wireOp",EDGE,"E150"),sQuery(id+"F6.wireOp",EDGE,"E151"),sQuery(id+"F6.wireOp",EDGE,"E152"),sQuery(id+"F6.wireOp",EDGE,"E153"),sQuery(id+"F6.wireOp",EDGE,"E154"),sQuery(id+"F6.wireOp",EDGE,"E155"),sQuery(id+"F6.wireOp",EDGE,"E156"),sQuery(id+"F6.wireOp",EDGE,"E157"),sQuery(id+"F6.wireOp",EDGE,"E158"),sQuery(id+"F6.wireOp",EDGE,"E159"),sQuery(id+"F6.wireOp",EDGE,"E160"),sQuery(id+"F6.wireOp",EDGE,"E161"),sQuery(id+"F6.wireOp",EDGE,"E162"),sQuery(id+"F6.wireOp",EDGE,"E163"),sQuery(id+"F6.wireOp",EDGE,"E164"),sQuery(id+"F6.wireOp",EDGE,"E165"),sQuery(id+"F6.wireOp",EDGE,"E166"),sQuery(id+"F6.wireOp",EDGE,"E167"),sQuery(id+"F6.wireOp",EDGE,"E168"),sQuery(id+"F6.wireOp",EDGE,"E169"),sQuery(id+"F6.wireOp",EDGE,"E170"),sQuery(id+"F6.wireOp",EDGE,"E171"),sQuery(id+"F6.wireOp",EDGE,"E172"),sQuery(id+"F6.wireOp",EDGE,"E173"),sQuery(id+"F6.wireOp",EDGE,"E174"),sQuery(id+"F6.wireOp",EDGE,"E175"),sQuery(id+"F6.wireOp",EDGE,"E176"),sQuery(id+"F6.wireOp",EDGE,"E177"),sQuery(id+"F6.wireOp",EDGE,"E178"),sQuery(id+"F6.wireOp",EDGE,"E179"),sQuery(id+"F6.wireOp",EDGE,"E180"),sQuery(id+"F6.wireOp",EDGE,"E181"),sQuery(id+"F6.wireOp",EDGE,"E182"),sQuery(id+"F6.wireOp",EDGE,"E183"),sQuery(id+"F6.wireOp",EDGE,"E184"),sQuery(id+"F6.wireOp",EDGE,"E185"),sQuery(id+"F6.wireOp",EDGE,"E186"),sQuery(id+"F6.wireOp",EDGE,"E187"),sQuery(id+"F6.wireOp",EDGE,"E188"),sQuery(id+"F6.wireOp",EDGE,"E189"),sQuery(id+"F6.wireOp",EDGE,"E190"),sQuery(id+"F6.wireOp",EDGE,"E191"),sQuery(id+"F6.wireOp",EDGE,"E192"),sQuery(id+"F6.wireOp",EDGE,"E193"),sQuery(id+"F6.wireOp",EDGE,"E194"),sQuery(id+"F6.wireOp",EDGE,"E195"),sQuery(id+"F6.wireOp",EDGE,"E196"),sQuery(id+"F6.wireOp",EDGE,"E197"),sQuery(id+"F6.wireOp",EDGE,"E198"),sQuery(id+"F6.wireOp",EDGE,"E199"),sQuery(id+"F6.wireOp",EDGE,"E200"),sQuery(id+"F6.wireOp",EDGE,"E201"),sQuery(id+"F6.wireOp",EDGE,"E202"),sQuery(id+"F6.wireOp",EDGE,"E203"),sQuery(id+"F6.wireOp",EDGE,"E204"),sQuery(id+"F6.wireOp",EDGE,"E205"),sQuery(id+"F6.wireOp",EDGE,"E206"),sQuery(id+"F6.wireOp",EDGE,"E207"),sQuery(id+"F6.wireOp",EDGE,"E208"),sQuery(id+"F6.wireOp",EDGE,"E209"),sQuery(id+"F6.wireOp",EDGE,"E210"),sQuery(id+"F6.wireOp",EDGE,"E211"),sQuery(id+"F6.wireOp",EDGE,"E212"),sQuery(id+"F6.wireOp",EDGE,"E213"),sQuery(id+"F6.wireOp",EDGE,"E214"),sQuery(id+"F6.wireOp",EDGE,"E215"),sQuery(id+"F6.wireOp",EDGE,"E216"),sQuery(id+"F6.wireOp",EDGE,"E217"),sQuery(id+"F6.wireOp",EDGE,"E218"),sQuery(id+"F6.wireOp",EDGE,"E219"),sQuery(id+"F6.wireOp",EDGE,"E220"),sQuery(id+"F6.wireOp",EDGE,"E221"),sQuery(id+"F6.wireOp",EDGE,"E222"),sQuery(id+"F6.wireOp",EDGE,"E223"),sQuery(id+"F6.wireOp",EDGE,"E224"),sQuery(id+"F6.wireOp",EDGE,"E225"),sQuery(id+"F6.wireOp",EDGE,"E226"),sQuery(id+"F6.wireOp",EDGE,"E227"),sQuery(id+"F6.wireOp",EDGE,"E228"),sQuery(id+"F6.wireOp",EDGE,"E229"),sQuery(id+"F6.wireOp",EDGE,"E230"),sQuery(id+"F6.wireOp",EDGE,"E231"),sQuery(id+"F6.wireOp",EDGE,"E232"),sQuery(id+"F6.wireOp",EDGE,"E233"),sQuery(id+"F6.wireOp",EDGE,"E234"),sQuery(id+"F6.wireOp",EDGE,"E235"),sQuery(id+"F6.wireOp",EDGE,"E236"),sQuery(id+"F6.wireOp",EDGE,"E237"),sQuery(id+"F6.wireOp",EDGE,"E238"),sQuery(id+"F6.wireOp",EDGE,"E239"),sQuery(id+"F6.wireOp",EDGE,"E240"),sQuery(id+"F6.wireOp",EDGE,"E241"),sQuery(id+"F6.wireOp",EDGE,"E242"),sQuery(id+"F6.wireOp",EDGE,"E243"),sQuery(id+"F6.wireOp",EDGE,"E244"),sQuery(id+"F6.wireOp",EDGE,"E245"),sQuery(id+"F6.wireOp",EDGE,"E246"),sQuery(id+"F6.wireOp",EDGE,"E247"),sQuery(id+"F6.wireOp",EDGE,"E248"),sQuery(id+"F6.wireOp",EDGE,"E249"),sQuery(id+"F6.wireOp",EDGE,"E250"),sQuery(id+"F6.wireOp",EDGE,"E251"),sQuery(id+"F6.wireOp",EDGE,"E252"),sQuery(id+"F6.wireOp",EDGE,"E253"),sQuery(id+"F6.wireOp",EDGE,"E254"),sQuery(id+"F6.wireOp",EDGE,"E255"),sQuery(id+"F6.wireOp",EDGE,"E256"),sQuery(id+"F6.wireOp",EDGE,"E257"),sQuery(id+"F6.wireOp",EDGE,"E258"),sQuery(id+"F6.wireOp",EDGE,"E259"),sQuery(id+"F6.wireOp",EDGE,"E260"),sQuery(id+"F6.wireOp",EDGE,"E261"),sQuery(id+"F6.wireOp",EDGE,"E262"),sQuery(id+"F6.wireOp",EDGE,"E263"),sQuery(id+"F6.wireOp",EDGE,"E264"),sQuery(id+"F6.wireOp",EDGE,"E265"),sQuery(id+"F6.wireOp",EDGE,"E266"),sQuery(id+"F6.wireOp",EDGE,"E267"),sQuery(id+"F6.wireOp",EDGE,"E268")])]});
            var Q1;
            {var subQ0=sQuery(id+"F0.wireOp",EDGE,"E0.top");Q1=makeQuery(id+"F2.opShell","OFFSET_EDGE",EDGE,{"disambiguationData":[OSD([subQ0]),TDD([makeQuery(id+"F1.opExtrude","CAP_EDGE",EDGE,{"disambiguationData":[OSD([subQ0])],"isStart":false})])]});}
            transform(context, id + "F8", {"entities" : qUnion([Q0]), "transformType" : TransformType.ROTATION, "transformAxis" : qUnion([Q1]), "angle" : 0 * degree, "makeCopy" : false});
        }
        {
            var Q0;
            Q0=makeQuery(id+"F7.opExtrude","SWEPT_BODY",BODY,{"disambiguationData":[OSD([sQuery(id+"F6.wireOp",EDGE,"E6"),sQuery(id+"F6.wireOp",EDGE,"E7"),sQuery(id+"F6.wireOp",EDGE,"E8"),sQuery(id+"F6.wireOp",EDGE,"E9"),sQuery(id+"F6.wireOp",EDGE,"E10"),sQuery(id+"F6.wireOp",EDGE,"E11"),sQuery(id+"F6.wireOp",EDGE,"E12"),sQuery(id+"F6.wireOp",EDGE,"E13"),sQuery(id+"F6.wireOp",EDGE,"E14"),sQuery(id+"F6.wireOp",EDGE,"E15"),sQuery(id+"F6.wireOp",EDGE,"E16"),sQuery(id+"F6.wireOp",EDGE,"E17"),sQuery(id+"F6.wireOp",EDGE,"E18"),sQuery(id+"F6.wireOp",EDGE,"E19"),sQuery(id+"F6.wireOp",EDGE,"E20"),sQuery(id+"F6.wireOp",EDGE,"E21"),sQuery(id+"F6.wireOp",EDGE,"E22"),sQuery(id+"F6.wireOp",EDGE,"E23"),sQuery(id+"F6.wireOp",EDGE,"E24"),sQuery(id+"F6.wireOp",EDGE,"E25"),sQuery(id+"F6.wireOp",EDGE,"E26"),sQuery(id+"F6.wireOp",EDGE,"E27"),sQuery(id+"F6.wireOp",EDGE,"E28"),sQuery(id+"F6.wireOp",EDGE,"E29"),sQuery(id+"F6.wireOp",EDGE,"E30"),sQuery(id+"F6.wireOp",EDGE,"E31"),sQuery(id+"F6.wireOp",EDGE,"E32"),sQuery(id+"F6.wireOp",EDGE,"E33"),sQuery(id+"F6.wireOp",EDGE,"E34"),sQuery(id+"F6.wireOp",EDGE,"E35"),sQuery(id+"F6.wireOp",EDGE,"E36"),sQuery(id+"F6.wireOp",EDGE,"E37"),sQuery(id+"F6.wireOp",EDGE,"E38"),sQuery(id+"F6.wireOp",EDGE,"E39"),sQuery(id+"F6.wireOp",EDGE,"E40"),sQuery(id+"F6.wireOp",EDGE,"E41"),sQuery(id+"F6.wireOp",EDGE,"E42"),sQuery(id+"F6.wireOp",EDGE,"E43"),sQuery(id+"F6.wireOp",EDGE,"E44"),sQuery(id+"F6.wireOp",EDGE,"E45"),sQuery(id+"F6.wireOp",EDGE,"E46"),sQuery(id+"F6.wireOp",EDGE,"E47"),sQuery(id+"F6.wireOp",EDGE,"E48"),sQuery(id+"F6.wireOp",EDGE,"E49"),sQuery(id+"F6.wireOp",EDGE,"E50"),sQuery(id+"F6.wireOp",EDGE,"E51"),sQuery(id+"F6.wireOp",EDGE,"E52"),sQuery(id+"F6.wireOp",EDGE,"E53"),sQuery(id+"F6.wireOp",EDGE,"E54"),sQuery(id+"F6.wireOp",EDGE,"E55"),sQuery(id+"F6.wireOp",EDGE,"E56"),sQuery(id+"F6.wireOp",EDGE,"E57"),sQuery(id+"F6.wireOp",EDGE,"E58"),sQuery(id+"F6.wireOp",EDGE,"E59"),sQuery(id+"F6.wireOp",EDGE,"E60"),sQuery(id+"F6.wireOp",EDGE,"E61"),sQuery(id+"F6.wireOp",EDGE,"E62"),sQuery(id+"F6.wireOp",EDGE,"E63"),sQuery(id+"F6.wireOp",EDGE,"E64"),sQuery(id+"F6.wireOp",EDGE,"E65"),sQuery(id+"F6.wireOp",EDGE,"E66"),sQuery(id+"F6.wireOp",EDGE,"E67"),sQuery(id+"F6.wireOp",EDGE,"E68"),sQuery(id+"F6.wireOp",EDGE,"E69"),sQuery(id+"F6.wireOp",EDGE,"E70"),sQuery(id+"F6.wireOp",EDGE,"E71"),sQuery(id+"F6.wireOp",EDGE,"E72"),sQuery(id+"F6.wireOp",EDGE,"E73"),sQuery(id+"F6.wireOp",EDGE,"E74"),sQuery(id+"F6.wireOp",EDGE,"E75"),sQuery(id+"F6.wireOp",EDGE,"E76"),sQuery(id+"F6.wireOp",EDGE,"E77"),sQuery(id+"F6.wireOp",EDGE,"E78"),sQuery(id+"F6.wireOp",EDGE,"E79"),sQuery(id+"F6.wireOp",EDGE,"E80"),sQuery(id+"F6.wireOp",EDGE,"E81"),sQuery(id+"F6.wireOp",EDGE,"E82"),sQuery(id+"F6.wireOp",EDGE,"E83"),sQuery(id+"F6.wireOp",EDGE,"E84"),sQuery(id+"F6.wireOp",EDGE,"E85"),sQuery(id+"F6.wireOp",EDGE,"E86"),sQuery(id+"F6.wireOp",EDGE,"E87"),sQuery(id+"F6.wireOp",EDGE,"E88"),sQuery(id+"F6.wireOp",EDGE,"E89"),sQuery(id+"F6.wireOp",EDGE,"E90"),sQuery(id+"F6.wireOp",EDGE,"E91"),sQuery(id+"F6.wireOp",EDGE,"E92"),sQuery(id+"F6.wireOp",EDGE,"E93"),sQuery(id+"F6.wireOp",EDGE,"E94"),sQuery(id+"F6.wireOp",EDGE,"E95"),sQuery(id+"F6.wireOp",EDGE,"E96"),sQuery(id+"F6.wireOp",EDGE,"E97"),sQuery(id+"F6.wireOp",EDGE,"E98"),sQuery(id+"F6.wireOp",EDGE,"E99"),sQuery(id+"F6.wireOp",EDGE,"E100"),sQuery(id+"F6.wireOp",EDGE,"E101"),sQuery(id+"F6.wireOp",EDGE,"E102"),sQuery(id+"F6.wireOp",EDGE,"E103"),sQuery(id+"F6.wireOp",EDGE,"E104"),sQuery(id+"F6.wireOp",EDGE,"E105"),sQuery(id+"F6.wireOp",EDGE,"E106"),sQuery(id+"F6.wireOp",EDGE,"E107"),sQuery(id+"F6.wireOp",EDGE,"E108"),sQuery(id+"F6.wireOp",EDGE,"E109"),sQuery(id+"F6.wireOp",EDGE,"E110"),sQuery(id+"F6.wireOp",EDGE,"E111"),sQuery(id+"F6.wireOp",EDGE,"E112"),sQuery(id+"F6.wireOp",EDGE,"E113"),sQuery(id+"F6.wireOp",EDGE,"E114"),sQuery(id+"F6.wireOp",EDGE,"E115"),sQuery(id+"F6.wireOp",EDGE,"E116"),sQuery(id+"F6.wireOp",EDGE,"E117"),sQuery(id+"F6.wireOp",EDGE,"E118"),sQuery(id+"F6.wireOp",EDGE,"E119"),sQuery(id+"F6.wireOp",EDGE,"E120"),sQuery(id+"F6.wireOp",EDGE,"E121"),sQuery(id+"F6.wireOp",EDGE,"E122"),sQuery(id+"F6.wireOp",EDGE,"E123"),sQuery(id+"F6.wireOp",EDGE,"E124"),sQuery(id+"F6.wireOp",EDGE,"E125"),sQuery(id+"F6.wireOp",EDGE,"E126"),sQuery(id+"F6.wireOp",EDGE,"E127"),sQuery(id+"F6.wireOp",EDGE,"E128"),sQuery(id+"F6.wireOp",EDGE,"E129"),sQuery(id+"F6.wireOp",EDGE,"E130"),sQuery(id+"F6.wireOp",EDGE,"E131"),sQuery(id+"F6.wireOp",EDGE,"E132"),sQuery(id+"F6.wireOp",EDGE,"E133"),sQuery(id+"F6.wireOp",EDGE,"E134"),sQuery(id+"F6.wireOp",EDGE,"E135"),sQuery(id+"F6.wireOp",EDGE,"E136"),sQuery(id+"F6.wireOp",EDGE,"E137"),sQuery(id+"F6.wireOp",EDGE,"E138"),sQuery(id+"F6.wireOp",EDGE,"E139"),sQuery(id+"F6.wireOp",EDGE,"E140"),sQuery(id+"F6.wireOp",EDGE,"E141"),sQuery(id+"F6.wireOp",EDGE,"E142"),sQuery(id+"F6.wireOp",EDGE,"E143"),sQuery(id+"F6.wireOp",EDGE,"E144"),sQuery(id+"F6.wireOp",EDGE,"E145"),sQuery(id+"F6.wireOp",EDGE,"E146"),sQuery(id+"F6.wireOp",EDGE,"E147"),sQuery(id+"F6.wireOp",EDGE,"E148"),sQuery(id+"F6.wireOp",EDGE,"E149"),sQuery(id+"F6.wireOp",EDGE,"E150"),sQuery(id+"F6.wireOp",EDGE,"E151"),sQuery(id+"F6.wireOp",EDGE,"E152"),sQuery(id+"F6.wireOp",EDGE,"E153"),sQuery(id+"F6.wireOp",EDGE,"E154"),sQuery(id+"F6.wireOp",EDGE,"E155"),sQuery(id+"F6.wireOp",EDGE,"E156"),sQuery(id+"F6.wireOp",EDGE,"E157"),sQuery(id+"F6.wireOp",EDGE,"E158"),sQuery(id+"F6.wireOp",EDGE,"E159"),sQuery(id+"F6.wireOp",EDGE,"E160"),sQuery(id+"F6.wireOp",EDGE,"E161"),sQuery(id+"F6.wireOp",EDGE,"E162"),sQuery(id+"F6.wireOp",EDGE,"E163"),sQuery(id+"F6.wireOp",EDGE,"E164"),sQuery(id+"F6.wireOp",EDGE,"E165"),sQuery(id+"F6.wireOp",EDGE,"E166"),sQuery(id+"F6.wireOp",EDGE,"E167"),sQuery(id+"F6.wireOp",EDGE,"E168"),sQuery(id+"F6.wireOp",EDGE,"E169"),sQuery(id+"F6.wireOp",EDGE,"E170"),sQuery(id+"F6.wireOp",EDGE,"E171"),sQuery(id+"F6.wireOp",EDGE,"E172"),sQuery(id+"F6.wireOp",EDGE,"E173"),sQuery(id+"F6.wireOp",EDGE,"E174"),sQuery(id+"F6.wireOp",EDGE,"E175"),sQuery(id+"F6.wireOp",EDGE,"E176"),sQuery(id+"F6.wireOp",EDGE,"E177"),sQuery(id+"F6.wireOp",EDGE,"E178"),sQuery(id+"F6.wireOp",EDGE,"E179"),sQuery(id+"F6.wireOp",EDGE,"E180"),sQuery(id+"F6.wireOp",EDGE,"E181"),sQuery(id+"F6.wireOp",EDGE,"E182"),sQuery(id+"F6.wireOp",EDGE,"E183"),sQuery(id+"F6.wireOp",EDGE,"E184"),sQuery(id+"F6.wireOp",EDGE,"E185"),sQuery(id+"F6.wireOp",EDGE,"E186"),sQuery(id+"F6.wireOp",EDGE,"E187"),sQuery(id+"F6.wireOp",EDGE,"E188"),sQuery(id+"F6.wireOp",EDGE,"E189"),sQuery(id+"F6.wireOp",EDGE,"E190"),sQuery(id+"F6.wireOp",EDGE,"E191"),sQuery(id+"F6.wireOp",EDGE,"E192"),sQuery(id+"F6.wireOp",EDGE,"E193"),sQuery(id+"F6.wireOp",EDGE,"E194"),sQuery(id+"F6.wireOp",EDGE,"E195"),sQuery(id+"F6.wireOp",EDGE,"E196"),sQuery(id+"F6.wireOp",EDGE,"E197"),sQuery(id+"F6.wireOp",EDGE,"E198"),sQuery(id+"F6.wireOp",EDGE,"E199"),sQuery(id+"F6.wireOp",EDGE,"E200"),sQuery(id+"F6.wireOp",EDGE,"E201"),sQuery(id+"F6.wireOp",EDGE,"E202"),sQuery(id+"F6.wireOp",EDGE,"E203"),sQuery(id+"F6.wireOp",EDGE,"E204"),sQuery(id+"F6.wireOp",EDGE,"E205"),sQuery(id+"F6.wireOp",EDGE,"E206"),sQuery(id+"F6.wireOp",EDGE,"E207"),sQuery(id+"F6.wireOp",EDGE,"E208"),sQuery(id+"F6.wireOp",EDGE,"E209"),sQuery(id+"F6.wireOp",EDGE,"E210"),sQuery(id+"F6.wireOp",EDGE,"E211"),sQuery(id+"F6.wireOp",EDGE,"E212"),sQuery(id+"F6.wireOp",EDGE,"E213"),sQuery(id+"F6.wireOp",EDGE,"E214"),sQuery(id+"F6.wireOp",EDGE,"E215"),sQuery(id+"F6.wireOp",EDGE,"E216"),sQuery(id+"F6.wireOp",EDGE,"E217"),sQuery(id+"F6.wireOp",EDGE,"E218"),sQuery(id+"F6.wireOp",EDGE,"E219"),sQuery(id+"F6.wireOp",EDGE,"E220"),sQuery(id+"F6.wireOp",EDGE,"E221"),sQuery(id+"F6.wireOp",EDGE,"E222"),sQuery(id+"F6.wireOp",EDGE,"E223"),sQuery(id+"F6.wireOp",EDGE,"E224"),sQuery(id+"F6.wireOp",EDGE,"E225"),sQuery(id+"F6.wireOp",EDGE,"E226"),sQuery(id+"F6.wireOp",EDGE,"E227"),sQuery(id+"F6.wireOp",EDGE,"E228"),sQuery(id+"F6.wireOp",EDGE,"E229"),sQuery(id+"F6.wireOp",EDGE,"E230"),sQuery(id+"F6.wireOp",EDGE,"E231"),sQuery(id+"F6.wireOp",EDGE,"E232"),sQuery(id+"F6.wireOp",EDGE,"E233"),sQuery(id+"F6.wireOp",EDGE,"E234"),sQuery(id+"F6.wireOp",EDGE,"E235"),sQuery(id+"F6.wireOp",EDGE,"E236"),sQuery(id+"F6.wireOp",EDGE,"E237"),sQuery(id+"F6.wireOp",EDGE,"E238"),sQuery(id+"F6.wireOp",EDGE,"E239"),sQuery(id+"F6.wireOp",EDGE,"E240"),sQuery(id+"F6.wireOp",EDGE,"E241"),sQuery(id+"F6.wireOp",EDGE,"E242"),sQuery(id+"F6.wireOp",EDGE,"E243"),sQuery(id+"F6.wireOp",EDGE,"E244"),sQuery(id+"F6.wireOp",EDGE,"E245"),sQuery(id+"F6.wireOp",EDGE,"E246"),sQuery(id+"F6.wireOp",EDGE,"E247"),sQuery(id+"F6.wireOp",EDGE,"E248"),sQuery(id+"F6.wireOp",EDGE,"E249"),sQuery(id+"F6.wireOp",EDGE,"E250"),sQuery(id+"F6.wireOp",EDGE,"E251"),sQuery(id+"F6.wireOp",EDGE,"E252"),sQuery(id+"F6.wireOp",EDGE,"E253"),sQuery(id+"F6.wireOp",EDGE,"E254"),sQuery(id+"F6.wireOp",EDGE,"E255"),sQuery(id+"F6.wireOp",EDGE,"E256"),sQuery(id+"F6.wireOp",EDGE,"E257"),sQuery(id+"F6.wireOp",EDGE,"E258"),sQuery(id+"F6.wireOp",EDGE,"E259"),sQuery(id+"F6.wireOp",EDGE,"E260"),sQuery(id+"F6.wireOp",EDGE,"E261"),sQuery(id+"F6.wireOp",EDGE,"E262"),sQuery(id+"F6.wireOp",EDGE,"E263"),sQuery(id+"F6.wireOp",EDGE,"E264"),sQuery(id+"F6.wireOp",EDGE,"E265"),sQuery(id+"F6.wireOp",EDGE,"E266"),sQuery(id+"F6.wireOp",EDGE,"E267"),sQuery(id+"F6.wireOp",EDGE,"E268")])]});
            var Q1;
            Q1=makeQuery(id+"F7.opExtrude","CAP_VERTEX",VERTEX,{"disambiguationData":[OSD([sQuery(id+"F6.wireOp",EDGE,"E6"),sQuery(id+"F6.wireOp",EDGE,"E268")])],"isStart":false});
            transform(context, id + "F9", {"entities" : qUnion([Q0]), "transformType" : TransformType.SCALE_UNIFORMLY, "scale" : 0.25, "scalePoint" : qUnion([Q1]), "makeCopy" : false});
        }
        {
            var Q0;
            Q0=makeQuery(id+"F1.opExtrude","SWEPT_FACE",FACE,{"disambiguationData":[OSD([sQuery(id+"F0.wireOp",EDGE,"E0.left")])]});
            var sketch = newSketch(context, id + "F10", { "sketchPlane" : qUnion([Q0])});
            skText(sketch, "E269", { "text": "Danger", "fontName": "OpenSans-Bold.ttf"});
            const initialGuessF10  = {"E269": [0.01833, 0.01675, 0, -1, 0.00417]};
            skSetInitialGuess(sketch, initialGuessF10);
            skSolve(sketch);
        }
        {
            var Q0;
            Q0 = qSketchRegion(id + "F10", true);
            extrude(context, id + "F11", {"entities" : qUnion([Q0]), "operationType" : NewBodyOperationType.ADD, "endBound" : BoundingType.SYMMETRIC, "depth" : 2.5 * mm, "offsetDistance" : 25 * mm});
        }
        {
            var Q0;
            Q0=makeQuery(id+"F1.opExtrude","SWEPT_BODY",BODY,{"disambiguationData":[OSD([sQuery(id+"F0.wireOp",EDGE,"E0.bottom"),sQuery(id+"F0.wireOp",EDGE,"E0.top"),sQuery(id+"F0.wireOp",EDGE,"E0.left"),sQuery(id+"F0.wireOp",EDGE,"E0.right")])]});
            var Q1;
            {var subQ0=sQuery(id+"F0.wireOp",EDGE,"E0.top");Q1=makeQuery(id+"F2.opShell","OFFSET_EDGE",EDGE,{"disambiguationData":[OSD([subQ0]),TDD([makeQuery(id+"F1.opExtrude","CAP_EDGE",EDGE,{"disambiguationData":[OSD([subQ0])],"isStart":false})])]});}
            transform(context, id + "F12", {"entities" : qUnion([Q0]), "transformType" : TransformType.ROTATION, "transformAxis" : qUnion([Q1]), "angle" : 90 * degree, "oppositeDirection" : true, "makeCopy" : false});
        }
        {
            var Q0;
            Q0=makeQuery(id+"F7.opExtrude","SWEPT_BODY",BODY,{"disambiguationData":[OSD([sQuery(id+"F6.wireOp",EDGE,"E6"),sQuery(id+"F6.wireOp",EDGE,"E7"),sQuery(id+"F6.wireOp",EDGE,"E8"),sQuery(id+"F6.wireOp",EDGE,"E9"),sQuery(id+"F6.wireOp",EDGE,"E10"),sQuery(id+"F6.wireOp",EDGE,"E11"),sQuery(id+"F6.wireOp",EDGE,"E12"),sQuery(id+"F6.wireOp",EDGE,"E13"),sQuery(id+"F6.wireOp",EDGE,"E14"),sQuery(id+"F6.wireOp",EDGE,"E15"),sQuery(id+"F6.wireOp",EDGE,"E16"),sQuery(id+"F6.wireOp",EDGE,"E17"),sQuery(id+"F6.wireOp",EDGE,"E18"),sQuery(id+"F6.wireOp",EDGE,"E19"),sQuery(id+"F6.wireOp",EDGE,"E20"),sQuery(id+"F6.wireOp",EDGE,"E21"),sQuery(id+"F6.wireOp",EDGE,"E22"),sQuery(id+"F6.wireOp",EDGE,"E23"),sQuery(id+"F6.wireOp",EDGE,"E24"),sQuery(id+"F6.wireOp",EDGE,"E25"),sQuery(id+"F6.wireOp",EDGE,"E26"),sQuery(id+"F6.wireOp",EDGE,"E27"),sQuery(id+"F6.wireOp",EDGE,"E28"),sQuery(id+"F6.wireOp",EDGE,"E29"),sQuery(id+"F6.wireOp",EDGE,"E30"),sQuery(id+"F6.wireOp",EDGE,"E31"),sQuery(id+"F6.wireOp",EDGE,"E32"),sQuery(id+"F6.wireOp",EDGE,"E33"),sQuery(id+"F6.wireOp",EDGE,"E34"),sQuery(id+"F6.wireOp",EDGE,"E35"),sQuery(id+"F6.wireOp",EDGE,"E36"),sQuery(id+"F6.wireOp",EDGE,"E37"),sQuery(id+"F6.wireOp",EDGE,"E38"),sQuery(id+"F6.wireOp",EDGE,"E39"),sQuery(id+"F6.wireOp",EDGE,"E40"),sQuery(id+"F6.wireOp",EDGE,"E41"),sQuery(id+"F6.wireOp",EDGE,"E42"),sQuery(id+"F6.wireOp",EDGE,"E43"),sQuery(id+"F6.wireOp",EDGE,"E44"),sQuery(id+"F6.wireOp",EDGE,"E45"),sQuery(id+"F6.wireOp",EDGE,"E46"),sQuery(id+"F6.wireOp",EDGE,"E47"),sQuery(id+"F6.wireOp",EDGE,"E48"),sQuery(id+"F6.wireOp",EDGE,"E49"),sQuery(id+"F6.wireOp",EDGE,"E50"),sQuery(id+"F6.wireOp",EDGE,"E51"),sQuery(id+"F6.wireOp",EDGE,"E52"),sQuery(id+"F6.wireOp",EDGE,"E53"),sQuery(id+"F6.wireOp",EDGE,"E54"),sQuery(id+"F6.wireOp",EDGE,"E55"),sQuery(id+"F6.wireOp",EDGE,"E56"),sQuery(id+"F6.wireOp",EDGE,"E57"),sQuery(id+"F6.wireOp",EDGE,"E58"),sQuery(id+"F6.wireOp",EDGE,"E59"),sQuery(id+"F6.wireOp",EDGE,"E60"),sQuery(id+"F6.wireOp",EDGE,"E61"),sQuery(id+"F6.wireOp",EDGE,"E62"),sQuery(id+"F6.wireOp",EDGE,"E63"),sQuery(id+"F6.wireOp",EDGE,"E64"),sQuery(id+"F6.wireOp",EDGE,"E65"),sQuery(id+"F6.wireOp",EDGE,"E66"),sQuery(id+"F6.wireOp",EDGE,"E67"),sQuery(id+"F6.wireOp",EDGE,"E68"),sQuery(id+"F6.wireOp",EDGE,"E69"),sQuery(id+"F6.wireOp",EDGE,"E70"),sQuery(id+"F6.wireOp",EDGE,"E71"),sQuery(id+"F6.wireOp",EDGE,"E72"),sQuery(id+"F6.wireOp",EDGE,"E73"),sQuery(id+"F6.wireOp",EDGE,"E74"),sQuery(id+"F6.wireOp",EDGE,"E75"),sQuery(id+"F6.wireOp",EDGE,"E76"),sQuery(id+"F6.wireOp",EDGE,"E77"),sQuery(id+"F6.wireOp",EDGE,"E78"),sQuery(id+"F6.wireOp",EDGE,"E79"),sQuery(id+"F6.wireOp",EDGE,"E80"),sQuery(id+"F6.wireOp",EDGE,"E81"),sQuery(id+"F6.wireOp",EDGE,"E82"),sQuery(id+"F6.wireOp",EDGE,"E83"),sQuery(id+"F6.wireOp",EDGE,"E84"),sQuery(id+"F6.wireOp",EDGE,"E85"),sQuery(id+"F6.wireOp",EDGE,"E86"),sQuery(id+"F6.wireOp",EDGE,"E87"),sQuery(id+"F6.wireOp",EDGE,"E88"),sQuery(id+"F6.wireOp",EDGE,"E89"),sQuery(id+"F6.wireOp",EDGE,"E90"),sQuery(id+"F6.wireOp",EDGE,"E91"),sQuery(id+"F6.wireOp",EDGE,"E92"),sQuery(id+"F6.wireOp",EDGE,"E93"),sQuery(id+"F6.wireOp",EDGE,"E94"),sQuery(id+"F6.wireOp",EDGE,"E95"),sQuery(id+"F6.wireOp",EDGE,"E96"),sQuery(id+"F6.wireOp",EDGE,"E97"),sQuery(id+"F6.wireOp",EDGE,"E98"),sQuery(id+"F6.wireOp",EDGE,"E99"),sQuery(id+"F6.wireOp",EDGE,"E100"),sQuery(id+"F6.wireOp",EDGE,"E101"),sQuery(id+"F6.wireOp",EDGE,"E102"),sQuery(id+"F6.wireOp",EDGE,"E103"),sQuery(id+"F6.wireOp",EDGE,"E104"),sQuery(id+"F6.wireOp",EDGE,"E105"),sQuery(id+"F6.wireOp",EDGE,"E106"),sQuery(id+"F6.wireOp",EDGE,"E107"),sQuery(id+"F6.wireOp",EDGE,"E108"),sQuery(id+"F6.wireOp",EDGE,"E109"),sQuery(id+"F6.wireOp",EDGE,"E110"),sQuery(id+"F6.wireOp",EDGE,"E111"),sQuery(id+"F6.wireOp",EDGE,"E112"),sQuery(id+"F6.wireOp",EDGE,"E113"),sQuery(id+"F6.wireOp",EDGE,"E114"),sQuery(id+"F6.wireOp",EDGE,"E115"),sQuery(id+"F6.wireOp",EDGE,"E116"),sQuery(id+"F6.wireOp",EDGE,"E117"),sQuery(id+"F6.wireOp",EDGE,"E118"),sQuery(id+"F6.wireOp",EDGE,"E119"),sQuery(id+"F6.wireOp",EDGE,"E120"),sQuery(id+"F6.wireOp",EDGE,"E121"),sQuery(id+"F6.wireOp",EDGE,"E122"),sQuery(id+"F6.wireOp",EDGE,"E123"),sQuery(id+"F6.wireOp",EDGE,"E124"),sQuery(id+"F6.wireOp",EDGE,"E125"),sQuery(id+"F6.wireOp",EDGE,"E126"),sQuery(id+"F6.wireOp",EDGE,"E127"),sQuery(id+"F6.wireOp",EDGE,"E128"),sQuery(id+"F6.wireOp",EDGE,"E129"),sQuery(id+"F6.wireOp",EDGE,"E130"),sQuery(id+"F6.wireOp",EDGE,"E131"),sQuery(id+"F6.wireOp",EDGE,"E132"),sQuery(id+"F6.wireOp",EDGE,"E133"),sQuery(id+"F6.wireOp",EDGE,"E134"),sQuery(id+"F6.wireOp",EDGE,"E135"),sQuery(id+"F6.wireOp",EDGE,"E136"),sQuery(id+"F6.wireOp",EDGE,"E137"),sQuery(id+"F6.wireOp",EDGE,"E138"),sQuery(id+"F6.wireOp",EDGE,"E139"),sQuery(id+"F6.wireOp",EDGE,"E140"),sQuery(id+"F6.wireOp",EDGE,"E141"),sQuery(id+"F6.wireOp",EDGE,"E142"),sQuery(id+"F6.wireOp",EDGE,"E143"),sQuery(id+"F6.wireOp",EDGE,"E144"),sQuery(id+"F6.wireOp",EDGE,"E145"),sQuery(id+"F6.wireOp",EDGE,"E146"),sQuery(id+"F6.wireOp",EDGE,"E147"),sQuery(id+"F6.wireOp",EDGE,"E148"),sQuery(id+"F6.wireOp",EDGE,"E149"),sQuery(id+"F6.wireOp",EDGE,"E150"),sQuery(id+"F6.wireOp",EDGE,"E151"),sQuery(id+"F6.wireOp",EDGE,"E152"),sQuery(id+"F6.wireOp",EDGE,"E153"),sQuery(id+"F6.wireOp",EDGE,"E154"),sQuery(id+"F6.wireOp",EDGE,"E155"),sQuery(id+"F6.wireOp",EDGE,"E156"),sQuery(id+"F6.wireOp",EDGE,"E157"),sQuery(id+"F6.wireOp",EDGE,"E158"),sQuery(id+"F6.wireOp",EDGE,"E159"),sQuery(id+"F6.wireOp",EDGE,"E160"),sQuery(id+"F6.wireOp",EDGE,"E161"),sQuery(id+"F6.wireOp",EDGE,"E162"),sQuery(id+"F6.wireOp",EDGE,"E163"),sQuery(id+"F6.wireOp",EDGE,"E164"),sQuery(id+"F6.wireOp",EDGE,"E165"),sQuery(id+"F6.wireOp",EDGE,"E166"),sQuery(id+"F6.wireOp",EDGE,"E167"),sQuery(id+"F6.wireOp",EDGE,"E168"),sQuery(id+"F6.wireOp",EDGE,"E169"),sQuery(id+"F6.wireOp",EDGE,"E170"),sQuery(id+"F6.wireOp",EDGE,"E171"),sQuery(id+"F6.wireOp",EDGE,"E172"),sQuery(id+"F6.wireOp",EDGE,"E173"),sQuery(id+"F6.wireOp",EDGE,"E174"),sQuery(id+"F6.wireOp",EDGE,"E175"),sQuery(id+"F6.wireOp",EDGE,"E176"),sQuery(id+"F6.wireOp",EDGE,"E177"),sQuery(id+"F6.wireOp",EDGE,"E178"),sQuery(id+"F6.wireOp",EDGE,"E179"),sQuery(id+"F6.wireOp",EDGE,"E180"),sQuery(id+"F6.wireOp",EDGE,"E181"),sQuery(id+"F6.wireOp",EDGE,"E182"),sQuery(id+"F6.wireOp",EDGE,"E183"),sQuery(id+"F6.wireOp",EDGE,"E184"),sQuery(id+"F6.wireOp",EDGE,"E185"),sQuery(id+"F6.wireOp",EDGE,"E186"),sQuery(id+"F6.wireOp",EDGE,"E187"),sQuery(id+"F6.wireOp",EDGE,"E188"),sQuery(id+"F6.wireOp",EDGE,"E189"),sQuery(id+"F6.wireOp",EDGE,"E190"),sQuery(id+"F6.wireOp",EDGE,"E191"),sQuery(id+"F6.wireOp",EDGE,"E192"),sQuery(id+"F6.wireOp",EDGE,"E193"),sQuery(id+"F6.wireOp",EDGE,"E194"),sQuery(id+"F6.wireOp",EDGE,"E195"),sQuery(id+"F6.wireOp",EDGE,"E196"),sQuery(id+"F6.wireOp",EDGE,"E197"),sQuery(id+"F6.wireOp",EDGE,"E198"),sQuery(id+"F6.wireOp",EDGE,"E199"),sQuery(id+"F6.wireOp",EDGE,"E200"),sQuery(id+"F6.wireOp",EDGE,"E201"),sQuery(id+"F6.wireOp",EDGE,"E202"),sQuery(id+"F6.wireOp",EDGE,"E203"),sQuery(id+"F6.wireOp",EDGE,"E204"),sQuery(id+"F6.wireOp",EDGE,"E205"),sQuery(id+"F6.wireOp",EDGE,"E206"),sQuery(id+"F6.wireOp",EDGE,"E207"),sQuery(id+"F6.wireOp",EDGE,"E208"),sQuery(id+"F6.wireOp",EDGE,"E209"),sQuery(id+"F6.wireOp",EDGE,"E210"),sQuery(id+"F6.wireOp",EDGE,"E211"),sQuery(id+"F6.wireOp",EDGE,"E212"),sQuery(id+"F6.wireOp",EDGE,"E213"),sQuery(id+"F6.wireOp",EDGE,"E214"),sQuery(id+"F6.wireOp",EDGE,"E215"),sQuery(id+"F6.wireOp",EDGE,"E216"),sQuery(id+"F6.wireOp",EDGE,"E217"),sQuery(id+"F6.wireOp",EDGE,"E218"),sQuery(id+"F6.wireOp",EDGE,"E219"),sQuery(id+"F6.wireOp",EDGE,"E220"),sQuery(id+"F6.wireOp",EDGE,"E221"),sQuery(id+"F6.wireOp",EDGE,"E222"),sQuery(id+"F6.wireOp",EDGE,"E223"),sQuery(id+"F6.wireOp",EDGE,"E224"),sQuery(id+"F6.wireOp",EDGE,"E225"),sQuery(id+"F6.wireOp",EDGE,"E226"),sQuery(id+"F6.wireOp",EDGE,"E227"),sQuery(id+"F6.wireOp",EDGE,"E228"),sQuery(id+"F6.wireOp",EDGE,"E229"),sQuery(id+"F6.wireOp",EDGE,"E230"),sQuery(id+"F6.wireOp",EDGE,"E231"),sQuery(id+"F6.wireOp",EDGE,"E232"),sQuery(id+"F6.wireOp",EDGE,"E233"),sQuery(id+"F6.wireOp",EDGE,"E234"),sQuery(id+"F6.wireOp",EDGE,"E235"),sQuery(id+"F6.wireOp",EDGE,"E236"),sQuery(id+"F6.wireOp",EDGE,"E237"),sQuery(id+"F6.wireOp",EDGE,"E238"),sQuery(id+"F6.wireOp",EDGE,"E239"),sQuery(id+"F6.wireOp",EDGE,"E240"),sQuery(id+"F6.wireOp",EDGE,"E241"),sQuery(id+"F6.wireOp",EDGE,"E242"),sQuery(id+"F6.wireOp",EDGE,"E243"),sQuery(id+"F6.wireOp",EDGE,"E244"),sQuery(id+"F6.wireOp",EDGE,"E245"),sQuery(id+"F6.wireOp",EDGE,"E246"),sQuery(id+"F6.wireOp",EDGE,"E247"),sQuery(id+"F6.wireOp",EDGE,"E248"),sQuery(id+"F6.wireOp",EDGE,"E249"),sQuery(id+"F6.wireOp",EDGE,"E250"),sQuery(id+"F6.wireOp",EDGE,"E251"),sQuery(id+"F6.wireOp",EDGE,"E252"),sQuery(id+"F6.wireOp",EDGE,"E253"),sQuery(id+"F6.wireOp",EDGE,"E254"),sQuery(id+"F6.wireOp",EDGE,"E255"),sQuery(id+"F6.wireOp",EDGE,"E256"),sQuery(id+"F6.wireOp",EDGE,"E257"),sQuery(id+"F6.wireOp",EDGE,"E258"),sQuery(id+"F6.wireOp",EDGE,"E259"),sQuery(id+"F6.wireOp",EDGE,"E260"),sQuery(id+"F6.wireOp",EDGE,"E261"),sQuery(id+"F6.wireOp",EDGE,"E262"),sQuery(id+"F6.wireOp",EDGE,"E263"),sQuery(id+"F6.wireOp",EDGE,"E264"),sQuery(id+"F6.wireOp",EDGE,"E265"),sQuery(id+"F6.wireOp",EDGE,"E266"),sQuery(id+"F6.wireOp",EDGE,"E267"),sQuery(id+"F6.wireOp",EDGE,"E268")])]});
            transform(context, id + "F13", {"entities" : qUnion([Q0]), "transformType" : TransformType.TRANSLATION_3D, "dx" : 0 * mm, "dy" : -50 * mm, "dz" : 3 * mm, "makeCopy" : false});
        }
        {
            var Q0;
            Q0=makeQuery(id+"F7.opExtrude","SWEPT_BODY",BODY,{"disambiguationData":[OSD([sQuery(id+"F6.wireOp",EDGE,"E6"),sQuery(id+"F6.wireOp",EDGE,"E7"),sQuery(id+"F6.wireOp",EDGE,"E8"),sQuery(id+"F6.wireOp",EDGE,"E9"),sQuery(id+"F6.wireOp",EDGE,"E10"),sQuery(id+"F6.wireOp",EDGE,"E11"),sQuery(id+"F6.wireOp",EDGE,"E12"),sQuery(id+"F6.wireOp",EDGE,"E13"),sQuery(id+"F6.wireOp",EDGE,"E14"),sQuery(id+"F6.wireOp",EDGE,"E15"),sQuery(id+"F6.wireOp",EDGE,"E16"),sQuery(id+"F6.wireOp",EDGE,"E17"),sQuery(id+"F6.wireOp",EDGE,"E18"),sQuery(id+"F6.wireOp",EDGE,"E19"),sQuery(id+"F6.wireOp",EDGE,"E20"),sQuery(id+"F6.wireOp",EDGE,"E21"),sQuery(id+"F6.wireOp",EDGE,"E22"),sQuery(id+"F6.wireOp",EDGE,"E23"),sQuery(id+"F6.wireOp",EDGE,"E24"),sQuery(id+"F6.wireOp",EDGE,"E25"),sQuery(id+"F6.wireOp",EDGE,"E26"),sQuery(id+"F6.wireOp",EDGE,"E27"),sQuery(id+"F6.wireOp",EDGE,"E28"),sQuery(id+"F6.wireOp",EDGE,"E29"),sQuery(id+"F6.wireOp",EDGE,"E30"),sQuery(id+"F6.wireOp",EDGE,"E31"),sQuery(id+"F6.wireOp",EDGE,"E32"),sQuery(id+"F6.wireOp",EDGE,"E33"),sQuery(id+"F6.wireOp",EDGE,"E34"),sQuery(id+"F6.wireOp",EDGE,"E35"),sQuery(id+"F6.wireOp",EDGE,"E36"),sQuery(id+"F6.wireOp",EDGE,"E37"),sQuery(id+"F6.wireOp",EDGE,"E38"),sQuery(id+"F6.wireOp",EDGE,"E39"),sQuery(id+"F6.wireOp",EDGE,"E40"),sQuery(id+"F6.wireOp",EDGE,"E41"),sQuery(id+"F6.wireOp",EDGE,"E42"),sQuery(id+"F6.wireOp",EDGE,"E43"),sQuery(id+"F6.wireOp",EDGE,"E44"),sQuery(id+"F6.wireOp",EDGE,"E45"),sQuery(id+"F6.wireOp",EDGE,"E46"),sQuery(id+"F6.wireOp",EDGE,"E47"),sQuery(id+"F6.wireOp",EDGE,"E48"),sQuery(id+"F6.wireOp",EDGE,"E49"),sQuery(id+"F6.wireOp",EDGE,"E50"),sQuery(id+"F6.wireOp",EDGE,"E51"),sQuery(id+"F6.wireOp",EDGE,"E52"),sQuery(id+"F6.wireOp",EDGE,"E53"),sQuery(id+"F6.wireOp",EDGE,"E54"),sQuery(id+"F6.wireOp",EDGE,"E55"),sQuery(id+"F6.wireOp",EDGE,"E56"),sQuery(id+"F6.wireOp",EDGE,"E57"),sQuery(id+"F6.wireOp",EDGE,"E58"),sQuery(id+"F6.wireOp",EDGE,"E59"),sQuery(id+"F6.wireOp",EDGE,"E60"),sQuery(id+"F6.wireOp",EDGE,"E61"),sQuery(id+"F6.wireOp",EDGE,"E62"),sQuery(id+"F6.wireOp",EDGE,"E63"),sQuery(id+"F6.wireOp",EDGE,"E64"),sQuery(id+"F6.wireOp",EDGE,"E65"),sQuery(id+"F6.wireOp",EDGE,"E66"),sQuery(id+"F6.wireOp",EDGE,"E67"),sQuery(id+"F6.wireOp",EDGE,"E68"),sQuery(id+"F6.wireOp",EDGE,"E69"),sQuery(id+"F6.wireOp",EDGE,"E70"),sQuery(id+"F6.wireOp",EDGE,"E71"),sQuery(id+"F6.wireOp",EDGE,"E72"),sQuery(id+"F6.wireOp",EDGE,"E73"),sQuery(id+"F6.wireOp",EDGE,"E74"),sQuery(id+"F6.wireOp",EDGE,"E75"),sQuery(id+"F6.wireOp",EDGE,"E76"),sQuery(id+"F6.wireOp",EDGE,"E77"),sQuery(id+"F6.wireOp",EDGE,"E78"),sQuery(id+"F6.wireOp",EDGE,"E79"),sQuery(id+"F6.wireOp",EDGE,"E80"),sQuery(id+"F6.wireOp",EDGE,"E81"),sQuery(id+"F6.wireOp",EDGE,"E82"),sQuery(id+"F6.wireOp",EDGE,"E83"),sQuery(id+"F6.wireOp",EDGE,"E84"),sQuery(id+"F6.wireOp",EDGE,"E85"),sQuery(id+"F6.wireOp",EDGE,"E86"),sQuery(id+"F6.wireOp",EDGE,"E87"),sQuery(id+"F6.wireOp",EDGE,"E88"),sQuery(id+"F6.wireOp",EDGE,"E89"),sQuery(id+"F6.wireOp",EDGE,"E90"),sQuery(id+"F6.wireOp",EDGE,"E91"),sQuery(id+"F6.wireOp",EDGE,"E92"),sQuery(id+"F6.wireOp",EDGE,"E93"),sQuery(id+"F6.wireOp",EDGE,"E94"),sQuery(id+"F6.wireOp",EDGE,"E95"),sQuery(id+"F6.wireOp",EDGE,"E96"),sQuery(id+"F6.wireOp",EDGE,"E97"),sQuery(id+"F6.wireOp",EDGE,"E98"),sQuery(id+"F6.wireOp",EDGE,"E99"),sQuery(id+"F6.wireOp",EDGE,"E100"),sQuery(id+"F6.wireOp",EDGE,"E101"),sQuery(id+"F6.wireOp",EDGE,"E102"),sQuery(id+"F6.wireOp",EDGE,"E103"),sQuery(id+"F6.wireOp",EDGE,"E104"),sQuery(id+"F6.wireOp",EDGE,"E105"),sQuery(id+"F6.wireOp",EDGE,"E106"),sQuery(id+"F6.wireOp",EDGE,"E107"),sQuery(id+"F6.wireOp",EDGE,"E108"),sQuery(id+"F6.wireOp",EDGE,"E109"),sQuery(id+"F6.wireOp",EDGE,"E110"),sQuery(id+"F6.wireOp",EDGE,"E111"),sQuery(id+"F6.wireOp",EDGE,"E112"),sQuery(id+"F6.wireOp",EDGE,"E113"),sQuery(id+"F6.wireOp",EDGE,"E114"),sQuery(id+"F6.wireOp",EDGE,"E115"),sQuery(id+"F6.wireOp",EDGE,"E116"),sQuery(id+"F6.wireOp",EDGE,"E117"),sQuery(id+"F6.wireOp",EDGE,"E118"),sQuery(id+"F6.wireOp",EDGE,"E119"),sQuery(id+"F6.wireOp",EDGE,"E120"),sQuery(id+"F6.wireOp",EDGE,"E121"),sQuery(id+"F6.wireOp",EDGE,"E122"),sQuery(id+"F6.wireOp",EDGE,"E123"),sQuery(id+"F6.wireOp",EDGE,"E124"),sQuery(id+"F6.wireOp",EDGE,"E125"),sQuery(id+"F6.wireOp",EDGE,"E126"),sQuery(id+"F6.wireOp",EDGE,"E127"),sQuery(id+"F6.wireOp",EDGE,"E128"),sQuery(id+"F6.wireOp",EDGE,"E129"),sQuery(id+"F6.wireOp",EDGE,"E130"),sQuery(id+"F6.wireOp",EDGE,"E131"),sQuery(id+"F6.wireOp",EDGE,"E132"),sQuery(id+"F6.wireOp",EDGE,"E133"),sQuery(id+"F6.wireOp",EDGE,"E134"),sQuery(id+"F6.wireOp",EDGE,"E135"),sQuery(id+"F6.wireOp",EDGE,"E136"),sQuery(id+"F6.wireOp",EDGE,"E137"),sQuery(id+"F6.wireOp",EDGE,"E138"),sQuery(id+"F6.wireOp",EDGE,"E139"),sQuery(id+"F6.wireOp",EDGE,"E140"),sQuery(id+"F6.wireOp",EDGE,"E141"),sQuery(id+"F6.wireOp",EDGE,"E142"),sQuery(id+"F6.wireOp",EDGE,"E143"),sQuery(id+"F6.wireOp",EDGE,"E144"),sQuery(id+"F6.wireOp",EDGE,"E145"),sQuery(id+"F6.wireOp",EDGE,"E146"),sQuery(id+"F6.wireOp",EDGE,"E147"),sQuery(id+"F6.wireOp",EDGE,"E148"),sQuery(id+"F6.wireOp",EDGE,"E149"),sQuery(id+"F6.wireOp",EDGE,"E150"),sQuery(id+"F6.wireOp",EDGE,"E151"),sQuery(id+"F6.wireOp",EDGE,"E152"),sQuery(id+"F6.wireOp",EDGE,"E153"),sQuery(id+"F6.wireOp",EDGE,"E154"),sQuery(id+"F6.wireOp",EDGE,"E155"),sQuery(id+"F6.wireOp",EDGE,"E156"),sQuery(id+"F6.wireOp",EDGE,"E157"),sQuery(id+"F6.wireOp",EDGE,"E158"),sQuery(id+"F6.wireOp",EDGE,"E159"),sQuery(id+"F6.wireOp",EDGE,"E160"),sQuery(id+"F6.wireOp",EDGE,"E161"),sQuery(id+"F6.wireOp",EDGE,"E162"),sQuery(id+"F6.wireOp",EDGE,"E163"),sQuery(id+"F6.wireOp",EDGE,"E164"),sQuery(id+"F6.wireOp",EDGE,"E165"),sQuery(id+"F6.wireOp",EDGE,"E166"),sQuery(id+"F6.wireOp",EDGE,"E167"),sQuery(id+"F6.wireOp",EDGE,"E168"),sQuery(id+"F6.wireOp",EDGE,"E169"),sQuery(id+"F6.wireOp",EDGE,"E170"),sQuery(id+"F6.wireOp",EDGE,"E171"),sQuery(id+"F6.wireOp",EDGE,"E172"),sQuery(id+"F6.wireOp",EDGE,"E173"),sQuery(id+"F6.wireOp",EDGE,"E174"),sQuery(id+"F6.wireOp",EDGE,"E175"),sQuery(id+"F6.wireOp",EDGE,"E176"),sQuery(id+"F6.wireOp",EDGE,"E177"),sQuery(id+"F6.wireOp",EDGE,"E178"),sQuery(id+"F6.wireOp",EDGE,"E179"),sQuery(id+"F6.wireOp",EDGE,"E180"),sQuery(id+"F6.wireOp",EDGE,"E181"),sQuery(id+"F6.wireOp",EDGE,"E182"),sQuery(id+"F6.wireOp",EDGE,"E183"),sQuery(id+"F6.wireOp",EDGE,"E184"),sQuery(id+"F6.wireOp",EDGE,"E185"),sQuery(id+"F6.wireOp",EDGE,"E186"),sQuery(id+"F6.wireOp",EDGE,"E187"),sQuery(id+"F6.wireOp",EDGE,"E188"),sQuery(id+"F6.wireOp",EDGE,"E189"),sQuery(id+"F6.wireOp",EDGE,"E190"),sQuery(id+"F6.wireOp",EDGE,"E191"),sQuery(id+"F6.wireOp",EDGE,"E192"),sQuery(id+"F6.wireOp",EDGE,"E193"),sQuery(id+"F6.wireOp",EDGE,"E194"),sQuery(id+"F6.wireOp",EDGE,"E195"),sQuery(id+"F6.wireOp",EDGE,"E196"),sQuery(id+"F6.wireOp",EDGE,"E197"),sQuery(id+"F6.wireOp",EDGE,"E198"),sQuery(id+"F6.wireOp",EDGE,"E199"),sQuery(id+"F6.wireOp",EDGE,"E200"),sQuery(id+"F6.wireOp",EDGE,"E201"),sQuery(id+"F6.wireOp",EDGE,"E202"),sQuery(id+"F6.wireOp",EDGE,"E203"),sQuery(id+"F6.wireOp",EDGE,"E204"),sQuery(id+"F6.wireOp",EDGE,"E205"),sQuery(id+"F6.wireOp",EDGE,"E206"),sQuery(id+"F6.wireOp",EDGE,"E207"),sQuery(id+"F6.wireOp",EDGE,"E208"),sQuery(id+"F6.wireOp",EDGE,"E209"),sQuery(id+"F6.wireOp",EDGE,"E210"),sQuery(id+"F6.wireOp",EDGE,"E211"),sQuery(id+"F6.wireOp",EDGE,"E212"),sQuery(id+"F6.wireOp",EDGE,"E213"),sQuery(id+"F6.wireOp",EDGE,"E214"),sQuery(id+"F6.wireOp",EDGE,"E215"),sQuery(id+"F6.wireOp",EDGE,"E216"),sQuery(id+"F6.wireOp",EDGE,"E217"),sQuery(id+"F6.wireOp",EDGE,"E218"),sQuery(id+"F6.wireOp",EDGE,"E219"),sQuery(id+"F6.wireOp",EDGE,"E220"),sQuery(id+"F6.wireOp",EDGE,"E221"),sQuery(id+"F6.wireOp",EDGE,"E222"),sQuery(id+"F6.wireOp",EDGE,"E223"),sQuery(id+"F6.wireOp",EDGE,"E224"),sQuery(id+"F6.wireOp",EDGE,"E225"),sQuery(id+"F6.wireOp",EDGE,"E226"),sQuery(id+"F6.wireOp",EDGE,"E227"),sQuery(id+"F6.wireOp",EDGE,"E228"),sQuery(id+"F6.wireOp",EDGE,"E229"),sQuery(id+"F6.wireOp",EDGE,"E230"),sQuery(id+"F6.wireOp",EDGE,"E231"),sQuery(id+"F6.wireOp",EDGE,"E232"),sQuery(id+"F6.wireOp",EDGE,"E233"),sQuery(id+"F6.wireOp",EDGE,"E234"),sQuery(id+"F6.wireOp",EDGE,"E235"),sQuery(id+"F6.wireOp",EDGE,"E236"),sQuery(id+"F6.wireOp",EDGE,"E237"),sQuery(id+"F6.wireOp",EDGE,"E238"),sQuery(id+"F6.wireOp",EDGE,"E239"),sQuery(id+"F6.wireOp",EDGE,"E240"),sQuery(id+"F6.wireOp",EDGE,"E241"),sQuery(id+"F6.wireOp",EDGE,"E242"),sQuery(id+"F6.wireOp",EDGE,"E243"),sQuery(id+"F6.wireOp",EDGE,"E244"),sQuery(id+"F6.wireOp",EDGE,"E245"),sQuery(id+"F6.wireOp",EDGE,"E246"),sQuery(id+"F6.wireOp",EDGE,"E247"),sQuery(id+"F6.wireOp",EDGE,"E248"),sQuery(id+"F6.wireOp",EDGE,"E249"),sQuery(id+"F6.wireOp",EDGE,"E250"),sQuery(id+"F6.wireOp",EDGE,"E251"),sQuery(id+"F6.wireOp",EDGE,"E252"),sQuery(id+"F6.wireOp",EDGE,"E253"),sQuery(id+"F6.wireOp",EDGE,"E254"),sQuery(id+"F6.wireOp",EDGE,"E255"),sQuery(id+"F6.wireOp",EDGE,"E256"),sQuery(id+"F6.wireOp",EDGE,"E257"),sQuery(id+"F6.wireOp",EDGE,"E258"),sQuery(id+"F6.wireOp",EDGE,"E259"),sQuery(id+"F6.wireOp",EDGE,"E260"),sQuery(id+"F6.wireOp",EDGE,"E261"),sQuery(id+"F6.wireOp",EDGE,"E262"),sQuery(id+"F6.wireOp",EDGE,"E263"),sQuery(id+"F6.wireOp",EDGE,"E264"),sQuery(id+"F6.wireOp",EDGE,"E265"),sQuery(id+"F6.wireOp",EDGE,"E266"),sQuery(id+"F6.wireOp",EDGE,"E267"),sQuery(id+"F6.wireOp",EDGE,"E268")])]});
            transform(context, id + "F14", {"entities" : qUnion([Q0]), "transformType" : TransformType.TRANSLATION_3D, "dx" : 6.3 * mm, "dy" : 0 * mm, "dz" : 0 * mm, "makeCopy" : false});
        }
        {
            var Q0;
            {var subQ1=sQuery(id+"F0.wireOp",EDGE,"E0.left");Q0=makeQuery(id+"F11.boolean.opBoolean","SPLIT",FACE,{"disambiguationData":[TD([makeQuery(id+"F11.opExtrude","SWEPT_FACE",FACE,{"disambiguationData":[OSD([sQuery(id+"F10.wireOp",EDGE,"E269.sketch_text.stroke-0")])]})])],"derivedFrom":makeQuery(id+"F1.opExtrude","SWEPT_FACE",FACE,{"disambiguationData":[OSD([subQ1])]})});}
            var sketch = newSketch(context, id + "F15", { "sketchPlane" : qUnion([Q0])});
            skText(sketch, "E270", { "text": "High", "fontName": "OpenSans-Bold.ttf"});
            skText(sketch, "E271", { "text": "Voltage", "fontName": "OpenSans-Bold.ttf"});
            const initialGuessF15  = {"E270": [0.0245, 0.00208, 1, 0, 0.00417], "E271": [0.0245, -0.00459, 1, 0, 0.00417]};
            skSetInitialGuess(sketch, initialGuessF15);
            skSolve(sketch);
        }
        {
            var Q0;
            Q0 = qSketchRegion(id + "F15", true);
            extrude(context, id + "F16", {"entities" : qUnion([Q0]), "operationType" : NewBodyOperationType.ADD, "endBound" : BoundingType.SYMMETRIC, "depth" : 2.5 * mm, "offsetDistance" : 25 * mm});
        }
        {
            var Q0;
            Q0=makeQuery(id+"F1.opExtrude","SWEPT_BODY",BODY,{"disambiguationData":[OSD([sQuery(id+"F0.wireOp",EDGE,"E0.bottom"),sQuery(id+"F0.wireOp",EDGE,"E0.top"),sQuery(id+"F0.wireOp",EDGE,"E0.left"),sQuery(id+"F0.wireOp",EDGE,"E0.right")])]});
            transform(context, id + "F17", {"entities" : qUnion([Q0]), "transformType" : TransformType.TRANSLATION_3D, "dx" : 0 * mm, "dy" : 40 * mm, "dz" : -5 * mm, "makeCopy" : false});
        }
        {
            var Q0;
            Q0=makeQuery(id+"F2.opShell","OFFSET_FACE",FACE,{"disambiguationData":[OSD([sQuery(id+"F0.wireOp",EDGE,"E0.top")])]});
            var sketch = newSketch(context, id + "F18", { "sketchPlane" : qUnion([Q0])});
            skLineSegment(sketch, "E272.bottom", {"start": v(-30.95, 2.75) * mm, "end": v(-18.95, 2.75) * mm});
            skLineSegment(sketch, "E272.top", {"start": v(-30.95, -9.25) * mm, "end": v(-18.95, -9.25) * mm});
            skLineSegment(sketch, "E272.left", {"start": v(-30.95, 2.75) * mm, "end": v(-30.95, -9.25) * mm});
            skLineSegment(sketch, "E272.right", {"start": v(-18.95, 2.75) * mm, "end": v(-18.95, -9.25) * mm});
            skSolve(sketch);
        }
        {
            var Q0;
            Q0 = qSketchRegion(id + "F18", true);
            extrude(context, id + "F19", {"entities" : qUnion([Q0]), "operationType" : NewBodyOperationType.REMOVE, "oppositeDirection" : true, "depth" : 25 * mm, "offsetDistance" : 25 * mm});
        }
        {
            var Q0;
            Q0=makeQuery(id+"F2.opShell","OFFSET_FACE",FACE,{"disambiguationData":[OSD([sQuery(id+"F0.wireOp",EDGE,"E0.bottom"),sQuery(id+"F0.wireOp",EDGE,"E0.top"),sQuery(id+"F0.wireOp",EDGE,"E0.left"),sQuery(id+"F0.wireOp",EDGE,"E0.right")])]});
            cPlane(context, id + "F20", {"entities" : qUnion([Q0]), "cplaneType" : CPlaneType.OFFSET, "offset" : 40 * mm, "width" : 150 * mm, "height" : 150 * mm});
        }
        {
            var Q0;
            Q0=qCreatedBy(id+"F20.planeOp",FACE);
            var sketch = newSketch(context, id + "F21", { "sketchPlane" : qUnion([Q0])});
            skLineSegment(sketch, "E273.bottom", {"start": v(36.54, -18.92) * mm, "end": v(-38.46, -18.92) * mm});
            skLineSegment(sketch, "E273.top", {"start": v(36.54, 18.58) * mm, "end": v(-38.46, 18.58) * mm});
            skLineSegment(sketch, "E273.left", {"start": v(36.54, -18.92) * mm, "end": v(36.54, 18.58) * mm});
            skLineSegment(sketch, "E273.right", {"start": v(-38.46, -18.92) * mm, "end": v(-38.46, 18.58) * mm});
            skSolve(sketch);
        }
        {
            var Q0;
            Q0 = qSketchRegion(id + "F21", true);
            extrude(context, id + "F22", {"entities" : qUnion([Q0]), "endBound" : BoundingType.SYMMETRIC, "depth" : 5 * mm, "offsetDistance" : 25 * mm});
        }
        {
            var Q0;
            Q0=makeQuery(id+"F22.opExtrude","SWEPT_EDGE",EDGE,{"disambiguationData":[OSD([sQuery(id+"F21.wireOp",EDGE,"E273.bottom"),sQuery(id+"F21.wireOp",EDGE,"E273.left")])]});
            var Q1;
            Q1=makeQuery(id+"F22.opExtrude","SWEPT_EDGE",EDGE,{"disambiguationData":[OSD([sQuery(id+"F21.wireOp",EDGE,"E273.bottom"),sQuery(id+"F21.wireOp",EDGE,"E273.right")])]});
            var Q2;
            Q2=makeQuery(id+"F22.opExtrude","SWEPT_EDGE",EDGE,{"disambiguationData":[OSD([sQuery(id+"F21.wireOp",EDGE,"E273.top"),sQuery(id+"F21.wireOp",EDGE,"E273.right")])]});
            var Q3;
            Q3=makeQuery(id+"F22.opExtrude","SWEPT_EDGE",EDGE,{"disambiguationData":[OSD([sQuery(id+"F21.wireOp",EDGE,"E273.top"),sQuery(id+"F21.wireOp",EDGE,"E273.left")])]});
            fillet(context, id + "F23", {"entities" : qUnion([Q0, Q1, Q2, Q3]), "radius" : 2 * mm, "tangentPropagation" : true, "allowEdgeOverflow" : false});
        }
        {
            var Q0;
            Q0=makeQuery(id+"F22.opExtrude","CAP_FACE",FACE,{"disambiguationData":[OSD([sQuery(id+"F21.wireOp",EDGE,"E273.bottom"),sQuery(id+"F21.wireOp",EDGE,"E273.top"),sQuery(id+"F21.wireOp",EDGE,"E273.left"),sQuery(id+"F21.wireOp",EDGE,"E273.right")])],"isStart":false});
            var sketch = newSketch(context, id + "F24", { "sketchPlane" : qUnion([Q0])});
            skLineSegment(sketch, "E274.bottom", {"start": v(-30.95, 12.58) * mm, "end": v(-20.95, 12.58) * mm});
            skLineSegment(sketch, "E274.top", {"start": v(-30.95, 5.08) * mm, "end": v(-20.95, 5.08) * mm});
            skLineSegment(sketch, "E274.left", {"start": v(-30.95, 12.58) * mm, "end": v(-30.95, 5.08) * mm});
            skLineSegment(sketch, "E274.right", {"start": v(-20.95, 12.58) * mm, "end": v(-20.95, 5.08) * mm});
            skSolve(sketch);
        }
        {
            var Q0;
            Q0 = qSketchRegion(id + "F24", true);
            extrude(context, id + "F25", {"entities" : qUnion([Q0]), "operationType" : NewBodyOperationType.REMOVE, "oppositeDirection" : true, "depth" : 10 * mm, "offsetDistance" : 25 * mm});
        }
        {
            var Q0;
            Q0=makeQuery(id+"F19.boolean.opBoolean","COPY",EDGE,{"derivedFrom":makeQuery(id+"F19.opExtrude","SWEPT_EDGE",EDGE,{"disambiguationData":[OSD([sQuery(id+"F18.wireOp",EDGE,"E272.bottom"),sQuery(id+"F18.wireOp",EDGE,"E272.right")])]})});
            var Q1;
            Q1=makeQuery(id+"F19.boolean.opBoolean","COPY",EDGE,{"derivedFrom":makeQuery(id+"F19.opExtrude","SWEPT_EDGE",EDGE,{"disambiguationData":[OSD([sQuery(id+"F18.wireOp",EDGE,"E272.bottom"),sQuery(id+"F18.wireOp",EDGE,"E272.left")])]})});
            fillet(context, id + "F26", {"entities" : qUnion([Q0, Q1]), "radius" : 6 * mm, "tangentPropagation" : true, "allowEdgeOverflow" : false});
        }
        {
            var Q0;
            Q0=makeQuery(id+"F19.boolean.opBoolean","COPY",EDGE,{"derivedFrom":makeQuery(id+"F19.opExtrude","SWEPT_EDGE",EDGE,{"disambiguationData":[OSD([sQuery(id+"F18.wireOp",EDGE,"E272.top"),sQuery(id+"F18.wireOp",EDGE,"E272.left")])]})});
            var Q1;
            Q1=makeQuery(id+"F19.boolean.opBoolean","COPY",EDGE,{"derivedFrom":makeQuery(id+"F19.opExtrude","SWEPT_EDGE",EDGE,{"disambiguationData":[OSD([sQuery(id+"F18.wireOp",EDGE,"E272.top"),sQuery(id+"F18.wireOp",EDGE,"E272.right")])]})});
            var Q2;
            Q2=makeQuery(id+"F25.boolean.opBoolean","COPY",EDGE,{"derivedFrom":makeQuery(id+"F25.opExtrude","SWEPT_EDGE",EDGE,{"disambiguationData":[OSD([sQuery(id+"F24.wireOp",EDGE,"E274.top"),sQuery(id+"F24.wireOp",EDGE,"E274.right")])]})});
            var Q3;
            Q3=makeQuery(id+"F25.boolean.opBoolean","COPY",EDGE,{"derivedFrom":makeQuery(id+"F25.opExtrude","SWEPT_EDGE",EDGE,{"disambiguationData":[OSD([sQuery(id+"F24.wireOp",EDGE,"E274.top"),sQuery(id+"F24.wireOp",EDGE,"E274.left")])]})});
            var Q4;
            Q4=makeQuery(id+"F25.boolean.opBoolean","COPY",EDGE,{"derivedFrom":makeQuery(id+"F25.opExtrude","SWEPT_EDGE",EDGE,{"disambiguationData":[OSD([sQuery(id+"F24.wireOp",EDGE,"E274.bottom"),sQuery(id+"F24.wireOp",EDGE,"E274.left")])]})});
            var Q5;
            Q5=makeQuery(id+"F25.boolean.opBoolean","COPY",EDGE,{"derivedFrom":makeQuery(id+"F25.opExtrude","SWEPT_EDGE",EDGE,{"disambiguationData":[OSD([sQuery(id+"F24.wireOp",EDGE,"E274.bottom"),sQuery(id+"F24.wireOp",EDGE,"E274.right")])]})});
            fillet(context, id + "F27", {"entities" : qUnion([Q0, Q1, Q2, Q3, Q4, Q5]), "radius" : 1 * mm, "tangentPropagation" : true, "allowEdgeOverflow" : false});
        }
        {
            var Q0;
            Q0=makeQuery(id+"F22.opExtrude","CAP_FACE",FACE,{"disambiguationData":[OSD([sQuery(id+"F21.wireOp",EDGE,"E273.bottom"),sQuery(id+"F21.wireOp",EDGE,"E273.top"),sQuery(id+"F21.wireOp",EDGE,"E273.left"),sQuery(id+"F21.wireOp",EDGE,"E273.right")])],"isStart":false});
            var sketch = newSketch(context, id + "F28", { "sketchPlane" : qUnion([Q0])});
            skText(sketch, "E275", { "text": "whitewater.io", "fontName": "OpenSans-Bold.ttf"});
            const initialGuessF28  = {"E275": [0.03254, 0.01458, -1, 0, 0.005]};
            skSetInitialGuess(sketch, initialGuessF28);
            skSolve(sketch);
        }
        {
            var Q0;
            Q0 = qSketchRegion(id + "F28", true);
            extrude(context, id + "F29", {"entities" : qUnion([Q0]), "operationType" : NewBodyOperationType.REMOVE, "endBound" : BoundingType.SYMMETRIC, "depth" : 2.4 * mm, "offsetDistance" : 25 * mm});
        }
        {
            var Q0;
            Q0=makeQuery(id+"F1.opExtrude","CAP_FACE",FACE,{"disambiguationData":[OSD([sQuery(id+"F0.wireOp",EDGE,"E0.bottom"),sQuery(id+"F0.wireOp",EDGE,"E0.top"),sQuery(id+"F0.wireOp",EDGE,"E0.left"),sQuery(id+"F0.wireOp",EDGE,"E0.right")])],"isStart":false});
            var sketch = newSketch(context, id + "F30", { "sketchPlane" : qUnion([Q0])});
            skArc(sketch, "E276", {"start": v(-27.15, -17.5) * mm, "mid": v(-25.52, -23) * mm, "end": v(-23.83, -17.5) * mm});
            skArc(sketch, "E277.MirrorCS", {"start": v(27.15, -17.5) * mm, "mid": v(25.52, -23) * mm, "end": v(23.83, -17.5) * mm});
            skArc(sketch, "E278", {"start": v(-12.5, 17.5) * mm, "mid": v(-15.5, 20.5) * mm, "end": v(-18.5, 17.5) * mm});
            skArc(sketch, "E279.MirrorCS", {"start": v(13.82, 15.02) * mm, "mid": v(15.52, 20.5) * mm, "end": v(17.16, 15) * mm});
            skPoint(sketch, "E280", {"position": v(-18.5, 17.5) * mm});
            skPoint(sketch, "E281", {"position": v(-12.5, 17.5) * mm});
            skPoint(sketch, "E282.orphan", {"position": v(-17.16, 15) * mm});
            skPoint(sketch, "E283.orphan", {"position": v(-13.82, 15.02) * mm});
            skSolve(sketch);
        }
        {
            var Q0;
            {var subQ0=sQuery(id+"F30.wireOp",EDGE,"E279.MirrorCS");var subQ1=makeQuery(id+"F1.opExtrude","CAP_EDGE",EDGE,{"disambiguationData":[OSD([sQuery(id+"F0.wireOp",EDGE,"E0.top")])],"isStart":false});var subQ2=makeQuery(id+"F30.imprint","INTERSECT",VERTEX,{"disambiguationData":[OD(0.0)],"derivedFrom":[subQ1,subQ0]});Q0=makeQuery(id+"F30.imprint","IMPRINT",FACE,{"disambiguationData":[TD([[makeQuery(id+"F30.imprint","IMPRINT",EDGE,{"disambiguationData":[TD([[subQ2,-1.0]])],"derivedFrom":subQ0}),-1.0]])]});}
            var Q1;
            {var subQ0=sQuery(id+"F30.wireOp",EDGE,"E277.MirrorCS");var subQ1=makeQuery(id+"F1.opExtrude","CAP_EDGE",EDGE,{"disambiguationData":[OSD([sQuery(id+"F0.wireOp",EDGE,"E0.bottom")])],"isStart":false});var subQ2=makeQuery(id+"F30.imprint","INTERSECT",VERTEX,{"disambiguationData":[OD(0.0)],"derivedFrom":[subQ1,subQ0]});Q1=makeQuery(id+"F30.imprint","IMPRINT",FACE,{"disambiguationData":[TD([[makeQuery(id+"F30.imprint","IMPRINT",EDGE,{"disambiguationData":[TD([[subQ2,1.0]])],"derivedFrom":subQ0}),-1.0]])]});}
            var Q2;
            {var subQ0=sQuery(id+"F30.wireOp",EDGE,"E276");var subQ1=makeQuery(id+"F1.opExtrude","CAP_EDGE",EDGE,{"disambiguationData":[OSD([sQuery(id+"F0.wireOp",EDGE,"E0.bottom")])],"isStart":false});var subQ2=makeQuery(id+"F30.imprint","INTERSECT",VERTEX,{"disambiguationData":[OD(0.0)],"derivedFrom":[subQ1,subQ0]});Q2=makeQuery(id+"F30.imprint","IMPRINT",FACE,{"disambiguationData":[TD([[makeQuery(id+"F30.imprint","IMPRINT",EDGE,{"disambiguationData":[TD([[subQ2,1.0]])],"derivedFrom":subQ0}),1.0]])]});}
            var Q3;
            {var subQ0=sQuery(id+"F30.wireOp",EDGE,"E278");var subQ1=makeQuery(id+"F1.opExtrude","CAP_EDGE",EDGE,{"disambiguationData":[OSD([sQuery(id+"F0.wireOp",EDGE,"E0.top")])],"isStart":false});var subQ2=makeQuery(id+"F30.imprint","INTERSECT",VERTEX,{"disambiguationData":[OD(0.0)],"derivedFrom":[subQ1,subQ0]});Q3=makeQuery(id+"F30.imprint","IMPRINT",FACE,{"disambiguationData":[TD([[makeQuery(id+"F30.imprint","IMPRINT",EDGE,{"disambiguationData":[TD([[subQ2,-1.0]])],"derivedFrom":subQ0}),1.0]])]});}
            extrude(context, id + "F31", {"entities" : qUnion([Q0, Q1, Q2, Q3]), "operationType" : NewBodyOperationType.ADD, "oppositeDirection" : true, "depth" : 25 * mm, "offsetDistance" : 25 * mm});
        }
        {
            var Q0;
            Q0=makeQuery(id+"F1.opExtrude","CAP_FACE",FACE,{"disambiguationData":[OSD([sQuery(id+"F0.wireOp",EDGE,"E0.bottom"),sQuery(id+"F0.wireOp",EDGE,"E0.top"),sQuery(id+"F0.wireOp",EDGE,"E0.left"),sQuery(id+"F0.wireOp",EDGE,"E0.right")])],"isStart":false});
            var sketch = newSketch(context, id + "F32", { "sketchPlane" : qUnion([Q0])});
            skPoint(sketch, "E284", {"position": v(-25.5, -20) * mm});
            skPoint(sketch, "E285", {"position": v(25.5, -20) * mm});
            skPoint(sketch, "E286", {"position": v(15.5, 17.5) * mm});
            skPoint(sketch, "E287", {"position": v(-15.5, 17.5) * mm});
            skSolve(sketch);
        }
        {
            var Q0;
            Q0=sQuery(id+"F32.wireOp",VERTEX,"8ecdf758-59be-45f3-8eae-b1de1c64d0ef");
            var Q1;
            Q1=sQuery(id+"F32.wireOp",VERTEX,"E286");
            var Q2;
            Q2=sQuery(id+"F32.wireOp",VERTEX,"E285");
            var Q3;
            Q3=sQuery(id+"F32.wireOp",VERTEX,"E284");
            var Q4;
            Q4=sQuery(id+"F32.wireOp",VERTEX,"E287");
            var Q5;
            Q5=makeQuery(id+"F1.opExtrude","SWEPT_BODY",BODY,{"disambiguationData":[OSD([sQuery(id+"F0.wireOp",EDGE,"E0.bottom"),sQuery(id+"F0.wireOp",EDGE,"E0.top"),sQuery(id+"F0.wireOp",EDGE,"E0.left"),sQuery(id+"F0.wireOp",EDGE,"E0.right")])]});
            var Q6;
            Q6=makeQuery(id+"F31.opExtrude","SWEPT_BODY",BODY,{"disambiguationData":[OSD([sQuery(id+"F0.wireOp",EDGE,"E0.bottom"),sQuery(id+"F30.wireOp",EDGE,"E276")])]});
            var Q7;
            Q7=makeQuery(id+"F31.opExtrude","SWEPT_BODY",BODY,{"disambiguationData":[OSD([sQuery(id+"F0.wireOp",EDGE,"E0.bottom"),sQuery(id+"F30.wireOp",EDGE,"E277.MirrorCS")])]});
            var Q8;
            Q8=makeQuery(id+"F31.opExtrude","SWEPT_BODY",BODY,{"disambiguationData":[OSD([sQuery(id+"F0.wireOp",EDGE,"E0.top"),sQuery(id+"F30.wireOp",EDGE,"E278")])]});
            var Q9;
            Q9=makeQuery(id+"F31.opExtrude","SWEPT_BODY",BODY,{"disambiguationData":[OSD([sQuery(id+"F0.wireOp",EDGE,"E0.top"),sQuery(id+"F30.wireOp",EDGE,"E279.MirrorCS")])]});
            hole(context, id + "F33", {"style" : HoleStyle.SIMPLE, "endStyle" : HoleEndStyle.BLIND, "standardTappedOrClearance" : lookupTablePath({ "standard" : "ISO", "engagement" : "75%", "pitch" : "0.5 mm", "size" : "M3", "type" : "Tapped" }), "standardBlindInLast" : lookupTablePath({ "standard" : "ISO", "engagement" : "75%", "pitch" : "0.5 mm", "size" : "M3", "type" : "Tapped" }), "holeDiameter" : 2.5 * mm, "majorDiameter" : 3 * mm, "showTappedDepth" : true, "holeDepth" : 13.5 * mm, "isTappedThrough" : true, "tappedDepth" : 12 * mm, "tapClearance" : 3, "startFromSketch" : true, "locations" : qUnion([Q0, Q1, Q2, Q3, Q4]), "scope" : qUnion([Q5, Q6, Q7, Q8, Q9])});
        }
        {
            var Q0;
            Q0=makeQuery(id+"F22.opExtrude","CAP_FACE",FACE,{"disambiguationData":[OSD([sQuery(id+"F21.wireOp",EDGE,"E273.bottom"),sQuery(id+"F21.wireOp",EDGE,"E273.top"),sQuery(id+"F21.wireOp",EDGE,"E273.left"),sQuery(id+"F21.wireOp",EDGE,"E273.right")])],"isStart":true});
            var sketch = newSketch(context, id + "F34", { "sketchPlane" : qUnion([Q0])});
            skCircle(sketch, "E288", {"center": v(-26.46, 18.92) * mm, "radius": 3 * mm});
            skCircle(sketch, "E289", {"center": v(24.54, 18.92) * mm, "radius": 3 * mm});
            skCircle(sketch, "E290", {"center": v(-14.46, -18.58) * mm, "radius": 3 * mm});
            skCircle(sketch, "E291", {"center": v(12.54, -18.58) * mm, "radius": 3 * mm});
            skSolve(sketch);
        }
        {
            var Q0;
            {var subQ0=sQuery(id+"F34.wireOp",EDGE,"E288");var subQ1=makeQuery(id+"F22.opExtrude","CAP_EDGE",EDGE,{"disambiguationData":[OSD([sQuery(id+"F21.wireOp",EDGE,"E273.bottom")])],"isStart":true});var subQ2=makeQuery(id+"F34.imprint","INTERSECT",VERTEX,{"disambiguationData":[OD(0.0)],"derivedFrom":[subQ1,subQ0]});Q0=makeQuery(id+"F34.imprint","IMPRINT",FACE,{"disambiguationData":[TD([[makeQuery(id+"F34.imprint","IMPRINT",EDGE,{"disambiguationData":[TD([[subQ2,1.0]])],"derivedFrom":subQ0}),1.0]])]});}
            var Q1;
            {var subQ0=sQuery(id+"F34.wireOp",EDGE,"E289");var subQ1=makeQuery(id+"F22.opExtrude","CAP_EDGE",EDGE,{"disambiguationData":[OSD([sQuery(id+"F21.wireOp",EDGE,"E273.bottom")])],"isStart":true});var subQ2=makeQuery(id+"F34.imprint","INTERSECT",VERTEX,{"disambiguationData":[OD(0.0)],"derivedFrom":[subQ1,subQ0]});Q1=makeQuery(id+"F34.imprint","IMPRINT",FACE,{"disambiguationData":[TD([[makeQuery(id+"F34.imprint","IMPRINT",EDGE,{"disambiguationData":[TD([[subQ2,1.0]])],"derivedFrom":subQ0}),1.0]])]});}
            var Q2;
            {var subQ0=sQuery(id+"F34.wireOp",EDGE,"E291");var subQ1=makeQuery(id+"F22.opExtrude","CAP_EDGE",EDGE,{"disambiguationData":[OSD([sQuery(id+"F21.wireOp",EDGE,"E273.top")])],"isStart":true});var subQ2=makeQuery(id+"F34.imprint","INTERSECT",VERTEX,{"disambiguationData":[OD(0.0)],"derivedFrom":[subQ1,subQ0]});Q2=makeQuery(id+"F34.imprint","IMPRINT",FACE,{"disambiguationData":[TD([[makeQuery(id+"F34.imprint","IMPRINT",EDGE,{"disambiguationData":[TD([[subQ2,1.0]])],"derivedFrom":subQ0}),1.0]])]});}
            var Q3;
            {var subQ0=sQuery(id+"F34.wireOp",EDGE,"E290");var subQ1=makeQuery(id+"F22.opExtrude","CAP_EDGE",EDGE,{"disambiguationData":[OSD([sQuery(id+"F21.wireOp",EDGE,"E273.top")])],"isStart":true});var subQ2=makeQuery(id+"F34.imprint","INTERSECT",VERTEX,{"disambiguationData":[OD(0.0)],"derivedFrom":[subQ1,subQ0]});Q3=makeQuery(id+"F34.imprint","IMPRINT",FACE,{"disambiguationData":[TD([[makeQuery(id+"F34.imprint","IMPRINT",EDGE,{"disambiguationData":[TD([[subQ2,-1.0]])],"derivedFrom":subQ0}),1.0]])]});}
            var Q4;
            {var subQ0=sQuery(id+"F34.wireOp",EDGE,"E289");var subQ1=makeQuery(id+"F22.opExtrude","CAP_EDGE",EDGE,{"disambiguationData":[OSD([sQuery(id+"F21.wireOp",EDGE,"E273.bottom")])],"isStart":true});var subQ2=makeQuery(id+"F34.imprint","INTERSECT",VERTEX,{"disambiguationData":[OD(0.0)],"derivedFrom":[subQ1,subQ0]});Q4=makeQuery(id+"F34.imprint","IMPRINT",FACE,{"disambiguationData":[TD([[makeQuery(id+"F34.imprint","IMPRINT",EDGE,{"disambiguationData":[TD([[subQ2,-1.0]])],"derivedFrom":subQ0}),1.0]])]});}
            extrude(context, id + "F35", {"entities" : qUnion([Q0, Q1, Q2, Q3, Q4]), "operationType" : NewBodyOperationType.ADD, "oppositeDirection" : true, "depth" : 5 * mm, "offsetDistance" : 25 * mm});
        }
        {
            var Q0;
            {var subQ4=sQuery(id+"F21.wireOp",EDGE,"E273.right");var subQ5=sQuery(id+"F21.wireOp",EDGE,"E273.bottom");var subQ6=sQuery(id+"F21.wireOp",EDGE,"E273.top");var subQ7=sQuery(id+"F21.wireOp",EDGE,"E273.left");Q0=makeQuery(id+"F29.boolean.opBoolean","SPLIT",FACE,{"disambiguationData":[TD([makeQuery(id+"F22.opExtrude","SWEPT_FACE",FACE,{"disambiguationData":[OSD([subQ5])]})])],"derivedFrom":makeQuery(id+"F22.opExtrude","CAP_FACE",FACE,{"disambiguationData":[OSD([subQ5,subQ6,subQ7,subQ4])],"isStart":false})});}
            cPlane(context, id + "F36", {"entities" : qUnion([Q0]), "cplaneType" : CPlaneType.OFFSET, "offset" : 0 * mm, "width" : 150 * mm, "height" : 150 * mm});
        }
        {
            var Q0;
            Q0=qCreatedBy(id+"F36.planeOp",FACE);
            var sketch = newSketch(context, id + "F37", { "sketchPlane" : qUnion([Q0])});
            skPoint(sketch, "E292", {"position": v(-14.46, 18.5) * mm});
            skPoint(sketch, "E293", {"position": v(12.54, 18.65) * mm});
            skPoint(sketch, "E294", {"position": v(-26.46, -18.94) * mm});
            skPoint(sketch, "E295", {"position": v(24.54, -18.94) * mm});
            skSolve(sketch);
        }
        {
            var Q0;
            Q0=sQuery(id+"F37.wireOp",VERTEX,"E292");
            var Q1;
            Q1=sQuery(id+"F37.wireOp",VERTEX,"E293");
            var Q2;
            Q2=sQuery(id+"F37.wireOp",VERTEX,"E295");
            var Q3;
            Q3=sQuery(id+"F37.wireOp",VERTEX,"E294");
            var Q4;
            Q4=makeQuery(id+"F22.opExtrude","SWEPT_BODY",BODY,{"disambiguationData":[OSD([sQuery(id+"F21.wireOp",EDGE,"E273.bottom"),sQuery(id+"F21.wireOp",EDGE,"E273.top"),sQuery(id+"F21.wireOp",EDGE,"E273.left"),sQuery(id+"F21.wireOp",EDGE,"E273.right")])]});
            hole(context, id + "F38", {"style" : HoleStyle.C_SINK, "endStyle" : HoleEndStyle.BLIND, "standardTappedOrClearance" : lookupTablePath({ "standard" : "ISO", "fit" : "Normal", "size" : "M3", "type" : "Clearance" }), "standardBlindInLast" : lookupTablePath({ "fit" : "Standard", "standard" : "ISO", "size" : "M3", "type" : "Clearance" }), "holeDiameter" : 3.3 * mm, "cSinkDiameter" : 6.72 * mm, "cSinkAngle" : 90 * degree, "majorDiameter" : 5 * mm, "holeDepth" : 8 * mm, "isTappedThrough" : true, "tappedDepth" : 12 * mm, "tapClearance" : 3, "startFromSketch" : true, "locations" : qUnion([Q0, Q1, Q2, Q3]), "scope" : qUnion([Q4])});
        }
        {
            var Q0;
            {var subQ0=sQuery(id+"F34.wireOp",EDGE,"E288");var subQ1=sQuery(id+"F21.wireOp",EDGE,"E273.bottom");var subQ2=sQuery(id+"F21.wireOp",EDGE,"E273.top");var subQ3=sQuery(id+"F34.wireOp",EDGE,"E289");Q0=makeQuery(id+"F35.boolean.opBoolean","SPLIT",EDGE,{"disambiguationData":[TD([makeQuery(id+"F22.opExtrude","SWEPT_FACE",FACE,{"disambiguationData":[OSD([subQ1])]}),makeQuery(id+"F22.opExtrude","CAP_FACE",FACE,{"disambiguationData":[OSD([subQ1,subQ2,sQuery(id+"F21.wireOp",EDGE,"E273.left"),sQuery(id+"F21.wireOp",EDGE,"E273.right")])],"isStart":false}),makeQuery(id+"F35.opExtrude","SWEPT_FACE",FACE,{"disambiguationData":[OSD([subQ0])]}),makeQuery(id+"F35.opExtrude","CAP_FACE",FACE,{"disambiguationData":[OSD([subQ1,subQ0])],"isStart":false}),makeQuery(id+"F35.opExtrude","SWEPT_FACE",FACE,{"disambiguationData":[OSD([subQ3])]}),makeQuery(id+"F35.opExtrude","CAP_FACE",FACE,{"disambiguationData":[OSD([subQ1,subQ3])],"isStart":false}),makeQuery(id+"F35.opExtrude","CAP_FACE",FACE,{"disambiguationData":[OSD([subQ2,sQuery(id+"F34.wireOp",EDGE,"E290")])],"isStart":false}),makeQuery(id+"F35.opExtrude","CAP_FACE",FACE,{"disambiguationData":[OSD([subQ2,sQuery(id+"F34.wireOp",EDGE,"E291")])],"isStart":false})])],"derivedFrom":makeQuery(id+"F22.opExtrude","CAP_EDGE",EDGE,{"disambiguationData":[OSD([subQ1])],"isStart":false})});}
            var Q1;
            {var subQ0=sQuery(id+"F21.wireOp",EDGE,"E273.bottom");var subQ1=sQuery(id+"F21.wireOp",EDGE,"E273.left");var subQ2=sQuery(id+"F34.wireOp",EDGE,"E289");var subQ3=sQuery(id+"F21.wireOp",EDGE,"E273.top");Q1=makeQuery(id+"F35.boolean.opBoolean","SPLIT",EDGE,{"disambiguationData":[TD([makeQuery(id+"F22.opExtrude","SWEPT_FACE",FACE,{"disambiguationData":[OSD([subQ0])]}),makeQuery(id+"F22.opExtrude","CAP_FACE",FACE,{"disambiguationData":[OSD([subQ0,subQ3,subQ1,sQuery(id+"F21.wireOp",EDGE,"E273.right")])],"isStart":false}),makeQuery(id+"F23.opFillet","BLEND_FACE",FACE,{"disambiguationData":[OSD([subQ0,subQ1])]}),makeQuery(id+"F35.opExtrude","CAP_FACE",FACE,{"disambiguationData":[OSD([subQ0,sQuery(id+"F34.wireOp",EDGE,"E288")])],"isStart":false}),makeQuery(id+"F35.opExtrude","SWEPT_FACE",FACE,{"disambiguationData":[OSD([subQ2])]}),makeQuery(id+"F35.opExtrude","CAP_FACE",FACE,{"disambiguationData":[OSD([subQ0,subQ2])],"isStart":false}),makeQuery(id+"F35.opExtrude","CAP_FACE",FACE,{"disambiguationData":[OSD([subQ3,sQuery(id+"F34.wireOp",EDGE,"E290")])],"isStart":false}),makeQuery(id+"F35.opExtrude","CAP_FACE",FACE,{"disambiguationData":[OSD([subQ3,sQuery(id+"F34.wireOp",EDGE,"E291")])],"isStart":false})])],"derivedFrom":makeQuery(id+"F22.opExtrude","CAP_EDGE",EDGE,{"disambiguationData":[OSD([subQ0])],"isStart":false})});}
            var Q2;
            {var subQ0=sQuery(id+"F21.wireOp",EDGE,"E273.left");var subQ1=sQuery(id+"F21.wireOp",EDGE,"E273.bottom");Q2=makeQuery(id+"F23.opFillet","BLEND_EDGE",EDGE,{"blendedFrom":[makeQuery(id+"F22.opExtrude","SWEPT_EDGE",EDGE,{"disambiguationData":[OSD([subQ1,subQ0])]}),makeQuery(id+"F22.opExtrude","CAP_FACE",FACE,{"disambiguationData":[OSD([subQ1,sQuery(id+"F21.wireOp",EDGE,"E273.top"),subQ0,sQuery(id+"F21.wireOp",EDGE,"E273.right")])],"isStart":false})],"blendedInto":[makeQuery(id+"F22.opExtrude","CAP_FACE",FACE,{"disambiguationData":[OSD([subQ1,sQuery(id+"F21.wireOp",EDGE,"E273.top"),subQ0,sQuery(id+"F21.wireOp",EDGE,"E273.right")])],"isStart":false})]});}
            var Q3;
            {var subQ0=sQuery(id+"F21.wireOp",EDGE,"E273.bottom");var subQ1=sQuery(id+"F21.wireOp",EDGE,"E273.top");var subQ2=sQuery(id+"F34.wireOp",EDGE,"E290");var subQ3=sQuery(id+"F34.wireOp",EDGE,"E291");Q3=makeQuery(id+"F35.boolean.opBoolean","SPLIT",EDGE,{"disambiguationData":[TD([makeQuery(id+"F22.opExtrude","CAP_FACE",FACE,{"disambiguationData":[OSD([subQ0,subQ1,sQuery(id+"F21.wireOp",EDGE,"E273.left"),sQuery(id+"F21.wireOp",EDGE,"E273.right")])],"isStart":false}),makeQuery(id+"F22.opExtrude","SWEPT_FACE",FACE,{"disambiguationData":[OSD([subQ1])]}),makeQuery(id+"F35.opExtrude","CAP_FACE",FACE,{"disambiguationData":[OSD([subQ0,sQuery(id+"F34.wireOp",EDGE,"E288")])],"isStart":false}),makeQuery(id+"F35.opExtrude","CAP_FACE",FACE,{"disambiguationData":[OSD([subQ0,sQuery(id+"F34.wireOp",EDGE,"E289")])],"isStart":false}),makeQuery(id+"F35.opExtrude","SWEPT_FACE",FACE,{"disambiguationData":[OSD([subQ2])]}),makeQuery(id+"F35.opExtrude","CAP_FACE",FACE,{"disambiguationData":[OSD([subQ1,subQ2])],"isStart":false}),makeQuery(id+"F35.opExtrude","SWEPT_FACE",FACE,{"disambiguationData":[OSD([subQ3])]}),makeQuery(id+"F35.opExtrude","CAP_FACE",FACE,{"disambiguationData":[OSD([subQ1,subQ3])],"isStart":false})])],"derivedFrom":makeQuery(id+"F22.opExtrude","CAP_EDGE",EDGE,{"disambiguationData":[OSD([subQ1])],"isStart":false})});}
            var Q4;
            {var subQ0=sQuery(id+"F21.wireOp",EDGE,"E273.bottom");var subQ1=sQuery(id+"F21.wireOp",EDGE,"E273.top");var subQ2=sQuery(id+"F21.wireOp",EDGE,"E273.right");var subQ3=sQuery(id+"F34.wireOp",EDGE,"E290");Q4=makeQuery(id+"F35.boolean.opBoolean","SPLIT",EDGE,{"disambiguationData":[TD([makeQuery(id+"F22.opExtrude","CAP_FACE",FACE,{"disambiguationData":[OSD([subQ0,subQ1,sQuery(id+"F21.wireOp",EDGE,"E273.left"),subQ2])],"isStart":false}),makeQuery(id+"F22.opExtrude","SWEPT_FACE",FACE,{"disambiguationData":[OSD([subQ1])]}),makeQuery(id+"F23.opFillet","BLEND_FACE",FACE,{"disambiguationData":[OSD([subQ1,subQ2])]}),makeQuery(id+"F35.opExtrude","CAP_FACE",FACE,{"disambiguationData":[OSD([subQ0,sQuery(id+"F34.wireOp",EDGE,"E288")])],"isStart":false}),makeQuery(id+"F35.opExtrude","CAP_FACE",FACE,{"disambiguationData":[OSD([subQ0,sQuery(id+"F34.wireOp",EDGE,"E289")])],"isStart":false}),makeQuery(id+"F35.opExtrude","SWEPT_FACE",FACE,{"disambiguationData":[OSD([subQ3])]}),makeQuery(id+"F35.opExtrude","CAP_FACE",FACE,{"disambiguationData":[OSD([subQ1,subQ3])],"isStart":false}),makeQuery(id+"F35.opExtrude","CAP_FACE",FACE,{"disambiguationData":[OSD([subQ1,sQuery(id+"F34.wireOp",EDGE,"E291")])],"isStart":false})])],"derivedFrom":makeQuery(id+"F22.opExtrude","CAP_EDGE",EDGE,{"disambiguationData":[OSD([subQ1])],"isStart":false})});}
            var Q5;
            {var subQ0=sQuery(id+"F21.wireOp",EDGE,"E273.right");var subQ1=sQuery(id+"F21.wireOp",EDGE,"E273.top");Q5=makeQuery(id+"F23.opFillet","BLEND_EDGE",EDGE,{"blendedFrom":[makeQuery(id+"F22.opExtrude","SWEPT_EDGE",EDGE,{"disambiguationData":[OSD([subQ1,subQ0])]}),makeQuery(id+"F22.opExtrude","CAP_FACE",FACE,{"disambiguationData":[OSD([sQuery(id+"F21.wireOp",EDGE,"E273.bottom"),subQ1,sQuery(id+"F21.wireOp",EDGE,"E273.left"),subQ0])],"isStart":false})],"blendedInto":[makeQuery(id+"F22.opExtrude","CAP_FACE",FACE,{"disambiguationData":[OSD([sQuery(id+"F21.wireOp",EDGE,"E273.bottom"),subQ1,sQuery(id+"F21.wireOp",EDGE,"E273.left"),subQ0])],"isStart":false})]});}
            fillet(context, id + "F39", {"entities" : qUnion([Q0, Q1, Q2, Q3, Q4, Q5]), "radius" : 2 * mm, "tangentPropagation" : true, "allowEdgeOverflow" : false});
        }
    });
